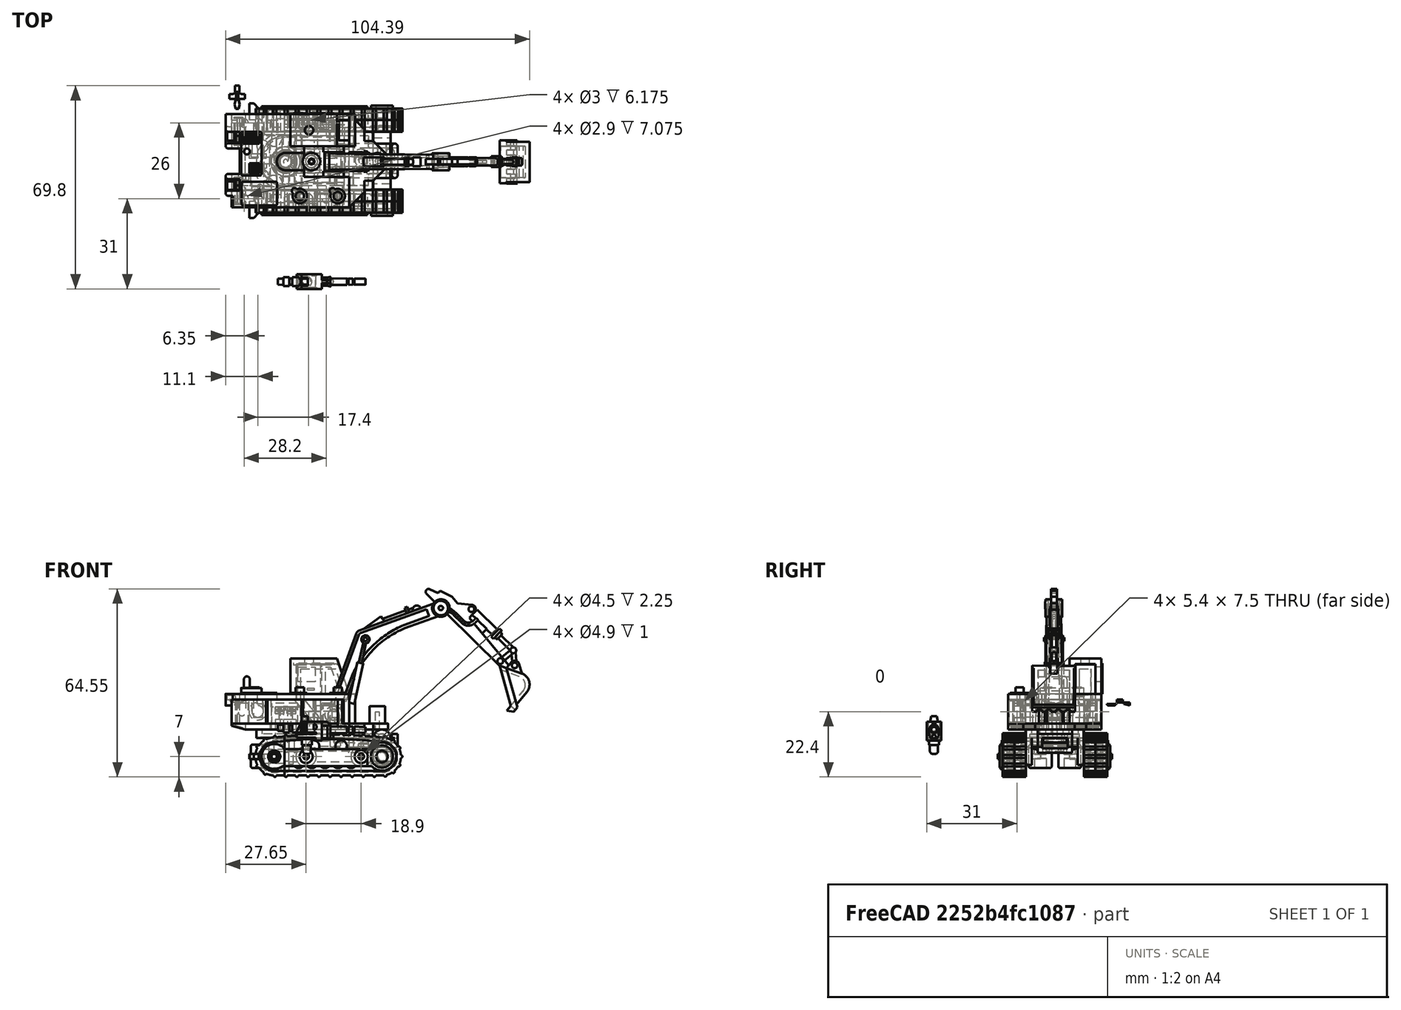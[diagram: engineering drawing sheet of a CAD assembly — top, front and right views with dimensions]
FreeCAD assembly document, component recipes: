
FREECAD ASSEMBLY — COMPONENT RECIPES ("Scavanger")

This assembly document has 15 components, labeled P0..P14 below (a component is one placed body or linked part). 15 of them carry a construction recipe — the FreeCAD feature program that regenerates the part from scratch, quoted from this document or its linked companion documents; the rest are supplied as boundary geometry only. No exploded tour is included for this assembly.
NOTE — document 2 of 4 of this assembly tour. The two overview renders and the header above are repeated from document 1; the component sections below continue where the previous document stopped.
COMPONENT P2 — recipe-attached ("Lower_Scoop", modeled in this document).
Construction recipe (the document's own serialized feature program — sketch geometry with constraints, then the solid features built on it; lengths are millimeters unless a unit is written):

FEATURE [Sketcher::SketchObject] Sketch065
  ArcFitTolerance = 1e-06
  AttachmentSupport = -> [XY_Plane002]
  FullyConstrained = true
  MakeInternals = false
  MapMode = 5
  sketch-geometry (12):
    g0: LineSegment [constr] StartX=-4e-16 StartY=0 StartZ=0 EndX=50.4 EndY=-4e-16 EndZ=0
    g1: LineSegment StartX=-4e-16 StartY=0 StartZ=0 EndX=25.1943 EndY=11.751 EndZ=0
    g2: LineSegment StartX=50.4 StartY=-4e-16 StartZ=0 EndX=25.1943 EndY=11.751 EndZ=0
    g3: LineSegment StartX=1.9444 StartY=-4.16885 StartZ=0 EndX=12.9214 EndY=0.950952 EndZ=0
    g4: ArcOfCircle CenterX=25.1943 CenterY=-29.2294 CenterZ=0 NormalX=0 NormalY=0 NormalZ=1 AngleXU=0 Radius=32.5803 StartAngle=1.18457 EndAngle=1.95703
    g5: LineSegment StartX=37.4673 StartY=0.950952 StartZ=0 EndX=48.4563 EndY=-4.16918 EndZ=0
    g6: LineSegment [constr] StartX=50.4 StartY=-4e-16 StartZ=0 EndX=48.4563 EndY=-4.16918 EndZ=0
    g7: LineSegment [constr] StartX=-4e-16 StartY=0 StartZ=0 EndX=1.9444 EndY=-4.16885 EndZ=0
    g8: LineSegment [constr] StartX=25.1943 StartY=-29.2294 StartZ=0 EndX=25.1943 EndY=3.35095 EndZ=0
    g9: LineSegment [constr] StartX=25.1943 StartY=3.35095 StartZ=0 EndX=25.1943 EndY=11.751 EndZ=0
    g10: ArcOfCircle CenterX=51.1739 CenterY=-2.89846 CenterZ=0 NormalX=0 NormalY=0 NormalZ=1 AngleXU=0 Radius=3 StartAngle=3.57898 EndAngle=8.1149
    g11: ArcOfCircle CenterX=-0.773401 CenterY=-2.89859 CenterZ=0 NormalX=0 NormalY=0 NormalZ=1 AngleXU=0 Radius=3 StartAngle=1.31005 EndAngle=5.84597
  constraints (35):
    c: Coincident(g0,g-1)
    c: PointOnObject(g0,g-1)
    c: Coincident(g1,g0)
    c: Coincident(g2,g0)
    c: Coincident(g2,g1)
    c: Angle(g1,g2) = 2.26893
    c: DistanceX(g0,g0) = 50.4
    c: Distance(g1) = 27.8
    c: Distance(g2) = 27.8102
    c: Coincident(g4,g3)
    c: Coincident(g5,g4)
    c: Coincident(g6,g0)
    c: Coincident(g6,g5)
    c: Distance(g6) = 4.6
    c: Coincident(g7,g0)
    c: Coincident(g7,g3)
    c: Distance(g7) = 4.6
    c: Coincident(g8,g4)
    c: PointOnObject(g8,g4)
    c: Vertical(g8)
    c: Coincident(g9,g8)
    c: Coincident(g9,g1)
    c: Vertical(g9)
    c: DistanceY(g9,g9) = 8.4
    c: Angle(g7,g1) = 1.5708
    c: Angle(g3,g7) = 1.5708
    c: DistanceY(g4,g3) = 0
    c: Angle(g2,g6) = 1.5708
    c: DistanceY(g3,g8) = 2.4
    c: Coincident(g10,g0)
    c: Coincident(g10,g5)
    c: Diameter(g10) = 6
    c: Coincident(g11,g0)
    c: Coincident(g11,g3)
    c: Diameter(g11) = 6
FEATURE [PartDesign::Pad] Pad038
  Direction = (0,0,1)
  Length = 5.6
  Length2 = 10
  Profile = -> Sketch065
  ReferenceAxis = -> Sketch065 [N_Axis]
  Refine = true
  Suppressed = false
  Type = 0
FEATURE [PartDesign::Fillet] Fillet003
  Base = -> Pad038 [Edge2]
  BaseFeature = -> Pad038
  Radius = 2
  Refine = true
  SupportTransform = false
  Suppressed = false
  UseAllEdges = false
FEATURE [Sketcher::SketchObject] Sketch066
  ArcFitTolerance = 1e-06
  AttachmentSupport = -> [Fillet003]
  ExternalGeometry = -> [Fillet003]
  FullyConstrained = true
  MakeInternals = false
  MapMode = 5
  Placement = pos=(0,0,0) rot=(1,0,0;3.14159rad)
  sketch-geometry (1):
    g0: Circle CenterX=51.1739 CenterY=2.89846 CenterZ=0 NormalX=0 NormalY=0 NormalZ=1 AngleXU=0 Radius=3
  constraints (2):
    c: Coincident(g0,g-3)
    c: Equal(g0,g-3)
FEATURE [PartDesign::Pad] Pad039
  BaseFeature = -> Fillet003
  Direction = (0,0,-1)
  Length = 0.25
  Length2 = 10
  Profile = -> Sketch066
  ReferenceAxis = -> Sketch066 [N_Axis]
  Refine = true
  Suppressed = false
  Type = 0
FEATURE [Sketcher::SketchObject] Sketch067
  ArcFitTolerance = 1e-06
  AttachmentSupport = -> [Pad039]
  ExternalGeometry = -> [Pad039]
  FullyConstrained = true
  MakeInternals = false
  MapMode = 5
  Placement = pos=(0,0,5.6) rot=(0,0,1;0rad)
  sketch-geometry (1):
    g0: Circle CenterX=51.1739 CenterY=-2.89846 CenterZ=0 NormalX=0 NormalY=0 NormalZ=1 AngleXU=0 Radius=3
  constraints (2):
    c: Coincident(g0,g-4)
    c: Equal(g0,g-4)
FEATURE [PartDesign::Pad] Pad040
  BaseFeature = -> Pad039
  Direction = (0,0,1)
  Length = 0.25
  Length2 = 10
  Profile = -> Sketch067
  ReferenceAxis = -> Sketch067 [N_Axis]
  Refine = true
  Suppressed = false
  Type = 0
FEATURE [Sketcher::SketchObject] Sketch068
  ArcFitTolerance = 1e-06
  AttachmentSupport = -> [Pad040]
  ExternalGeometry = -> [Pad040]
  FullyConstrained = true
  MakeInternals = false
  MapMode = 5
  Placement = pos=(0,0,5.6) rot=(0,0,1;0rad)
  sketch-geometry (1):
    g0: Circle CenterX=-0.773401 CenterY=-2.89859 CenterZ=0 NormalX=0 NormalY=0 NormalZ=1 AngleXU=0 Radius=3
  constraints (2):
    c: Coincident(g0,g-3)
    c: Equal(g0,g-3)
FEATURE [PartDesign::Pad] Pad041
  BaseFeature = -> Pad040
  Direction = (0,0,1)
  Length = 0.1
  Length2 = 10
  Profile = -> Sketch068
  ReferenceAxis = -> Sketch068 [N_Axis]
  Refine = true
  Suppressed = false
  Type = 0
FEATURE [Sketcher::SketchObject] Sketch069
  ArcFitTolerance = 1e-06
  AttachmentSupport = -> [Pad041]
  ExternalGeometry = -> [Pad041]
  FullyConstrained = true
  MakeInternals = false
  MapMode = 5
  Placement = pos=(0,0,0) rot=(1,0,0;3.14159rad)
  sketch-geometry (1):
    g0: Circle CenterX=-0.773401 CenterY=2.89859 CenterZ=0 NormalX=0 NormalY=0 NormalZ=1 AngleXU=0 Radius=3
  constraints (2):
    c: Coincident(g0,g-3)
    c: Equal(g0,g-3)
FEATURE [PartDesign::Pad] Pad042
  BaseFeature = -> Pad041
  Direction = (0,0,-1)
  Length = 0.1
  Length2 = 10
  Profile = -> Sketch069
  ReferenceAxis = -> Sketch069 [N_Axis]
  Refine = true
  Suppressed = false
  Type = 0
FEATURE [Sketcher::SketchObject] Sketch070
  ArcFitTolerance = 1e-06
  AttachmentSupport = -> [Pad042]
  ExternalGeometry = -> [Pad042]
  FullyConstrained = false
  MakeInternals = false
  MapMode = 5
  Placement = pos=(0,0,0) rot=(1,0,0;3.14159rad)
  sketch-geometry (4):
    g0: LineSegment StartX=24.0163 StartY=-5.17817 StartZ=0 EndX=24.0163 EndY=-6.67308 EndZ=0
    g1: LineSegment StartX=24.0163 StartY=-6.67308 StartZ=0 EndX=26.3302 EndY=-6.67308 EndZ=0
    g2: LineSegment StartX=26.3302 StartY=-6.67308 StartZ=0 EndX=26.3302 EndY=-5.17817 EndZ=0
    g3: LineSegment StartX=26.3302 StartY=-5.17817 StartZ=0 EndX=24.0163 EndY=-5.17817 EndZ=0
  constraints (8):
    c: Coincident(g0,g1)
    c: Coincident(g1,g2)
    c: Coincident(g2,g3)
    c: Coincident(g3,g0)
    c: Vertical(g0)
    c: Vertical(g2)
    c: Horizontal(g1)
    c: Horizontal(g3)
FEATURE [PartDesign::Pad] Pad043
  BaseFeature = -> Pad042
  Direction = (0,0,-1)
  Length = 1
  Length2 = 10
  Profile = -> Sketch070
  ReferenceAxis = -> Sketch070 [N_Axis]
  Refine = true
  Suppressed = false
  Type = 0
FEATURE [Sketcher::SketchObject] Sketch071
  ArcFitTolerance = 1e-06
  AttachmentOffset = pos=(0,0,-8) rot=(0,0,1;0rad)
  AttachmentSupport = -> [Pad043]
  ExternalGeometry = -> [Pad043]
  FullyConstrained = true
  MakeInternals = false
  MapMode = 5
  Placement = pos=(0,13.1782,-1.8e-15) rot=(1,0,0;1.5708rad)
  sketch-geometry (10):
    g0: LineSegment StartX=50.4 StartY=1e-16 StartZ=0 EndX=50.4 EndY=-2 EndZ=0
    g1: LineSegment StartX=50.4 StartY=-2 StartZ=0 EndX=0 EndY=-2 EndZ=0
    g2: LineSegment StartX=0 StartY=-2 StartZ=0 EndX=0 EndY=0 EndZ=0
    g3: LineSegment StartX=0 StartY=0 StartZ=0 EndX=-4e-16 EndY=0.4 EndZ=0
    g4: LineSegment StartX=-4e-16 StartY=0.4 StartZ=0 EndX=50.4 EndY=1e-16 EndZ=0
    g5: LineSegment StartX=0 StartY=5.6 StartZ=0 EndX=-4e-16 EndY=5.2 EndZ=0
    g6: LineSegment StartX=-4e-16 StartY=5.2 StartZ=0 EndX=50.4 EndY=5.6 EndZ=0
    g7: LineSegment StartX=50.4 StartY=5.6 StartZ=0 EndX=50.4 EndY=7.6 EndZ=0
    g8: LineSegment StartX=50.4 StartY=7.6 StartZ=0 EndX=0 EndY=7.6 EndZ=0
    g9: LineSegment StartX=0 StartY=5.6 StartZ=0 EndX=0 EndY=7.6 EndZ=0
  constraints (26):
    c: Coincident(g0,g-5)
    c: Vertical(g0)
    c: Coincident(g1,g0)
    c: Horizontal(g1)
    c: Coincident(g2,g1)
    c: Coincident(g2,g-1)
    c: Vertical(g2)
    c: Coincident(g3,g2)
    c: PointOnObject(g3,g-3)
    c: Coincident(g4,g3)
    c: Coincident(g4,g0)
    c: DistanceY(g3,g3) = 0.4
    c: DistanceY(g2,g2) = 2
    c: PointOnObject(g5,g-3)
    c: Coincident(g6,g5)
    c: DistanceY(g5,g5) = 0.4
    c: Coincident(g7,g6)
    c: Vertical(g7)
    c: Coincident(g8,g7)
    c: PointOnObject(g8,g-2)
    c: Horizontal(g8)
    c: Coincident(g9,g5)
    c: Coincident(g9,g8)
    c: DistanceY(g9,g9) = 2
    c: Coincident(g5,g-8)
    c: Coincident(g6,g-6)
FEATURE [PartDesign::Pocket] Pocket028
  BaseFeature = -> Pad043
  Direction = (0,1,-2e-16)
  Length = 22
  Length2 = 5
  Profile = -> Sketch071
  ReferenceAxis = -> Sketch071 [N_Axis]
  Refine = true
  Reversed = true
  Suppressed = false
  Type = 0
FEATURE [Sketcher::SketchObject] Sketch072
  ArcFitTolerance = 1e-06
  AttachmentSupport = -> [Pocket028]
  ExternalGeometry = -> [Pocket028]
  FullyConstrained = true
  MakeInternals = false
  MapMode = 5
  Placement = pos=(0,0,5.85) rot=(0,0,1;0rad)
  sketch-geometry (1):
    g0: Circle CenterX=51.1739 CenterY=-2.89846 CenterZ=0 NormalX=0 NormalY=0 NormalZ=1 AngleXU=0 Radius=3
  constraints (2):
    c: Coincident(g0,g-3)
    c: Equal(g0,g-3)
FEATURE [PartDesign::Pad] Pad044
  BaseFeature = -> Pocket028
  Direction = (0,0,1)
  Length = 6.1
  Length2 = 10
  Profile = -> Sketch072
  ReferenceAxis = -> Sketch072 [N_Axis]
  Refine = true
  Reversed = true
  Suppressed = false
  Type = 0
FEATURE [Sketcher::SketchObject] Sketch073
  ArcFitTolerance = 1e-06
  AttachmentSupport = -> [Pad044]
  ExternalGeometry = -> [Pad044]
  FullyConstrained = true
  MakeInternals = false
  MapMode = 5
  Placement = pos=(0,0,5.7) rot=(0,0,1;0rad)
  sketch-geometry (1):
    g0: Circle CenterX=-0.773401 CenterY=-2.89859 CenterZ=0 NormalX=0 NormalY=0 NormalZ=1 AngleXU=0 Radius=3
  constraints (2):
    c: Coincident(g0,g-3)
    c: Equal(g0,g-3)
FEATURE [PartDesign::Pad] Pad045
  BaseFeature = -> Pad044
  Direction = (0,0,1)
  Length = 5.8
  Length2 = 10
  Profile = -> Sketch073
  ReferenceAxis = -> Sketch073 [N_Axis]
  Refine = true
  Reversed = true
  Suppressed = false
  Type = 0
FEATURE [PartDesign::Pad] Pad046
  BaseFeature = -> Pad045
  Direction = (0,0,-1)
  Length = 0.25
  Length2 = 10
  Profile = -> Pad045 [Face1]
  Refine = true
  Suppressed = false
  Type = 0
FEATURE [PartDesign::Pad] Pad047
  BaseFeature = -> Pad046
  Direction = (0,0,1)
  Length = 0.25
  Length2 = 10
  Profile = -> Pad046 [Face1]
  Refine = true
  Suppressed = false
  Type = 0
FEATURE [Sketcher::SketchObject] Sketch074
  ArcFitTolerance = 1e-06
  AttachmentSupport = -> [Pad047]
  ExternalGeometry = -> [Pad047]
  FullyConstrained = true
  MakeInternals = false
  MapMode = 5
  Placement = pos=(0,0,6.1) rot=(0,0,1;0rad)
  sketch-geometry (1):
    g0: Circle CenterX=51.1739 CenterY=-2.89846 CenterZ=0 NormalX=0 NormalY=0 NormalZ=1 AngleXU=0 Radius=1.9
  constraints (2):
    c: Coincident(g0,g-3)
    c: Radius(g0) = 1.9
FEATURE [PartDesign::Pad] Pad048
  BaseFeature = -> Pad047
  Direction = (0,0,1)
  Length = 2
  Length2 = 10
  Profile = -> Sketch074
  ReferenceAxis = -> Sketch074 [N_Axis]
  Refine = true
  Suppressed = false
  Type = 0
FEATURE [Sketcher::SketchObject] Sketch075
  ArcFitTolerance = 1e-06
  AttachmentSupport = -> [Pad048]
  ExternalGeometry = -> [Pad048]
  FullyConstrained = true
  MakeInternals = false
  MapMode = 5
  Placement = pos=(0,0,-0.5) rot=(1,0,0;3.14159rad)
  sketch-geometry (1):
    g0: Circle CenterX=51.1739 CenterY=2.89846 CenterZ=0 NormalX=0 NormalY=0 NormalZ=1 AngleXU=0 Radius=1.9
  constraints (2):
    c: Coincident(g0,g-3)
    c: Radius(g0) = 1.9
FEATURE [PartDesign::Pad] Pad049
  BaseFeature = -> Pad048
  Direction = (0,0,-1)
  Length = 2
  Length2 = 10
  Profile = -> Sketch075
  ReferenceAxis = -> Sketch075 [N_Axis]
  Refine = true
  Suppressed = false
  Type = 0
FEATURE [Sketcher::SketchObject] Sketch076
  ArcFitTolerance = 1e-06
  AttachmentSupport = -> [Pad049]
  ExternalGeometry = -> [Pad049]
  FullyConstrained = true
  MakeInternals = false
  MapMode = 5
  Placement = pos=(0,0,5.7) rot=(0,0,1;0rad)
  sketch-geometry (1):
    g0: Circle CenterX=-0.773401 CenterY=-2.89859 CenterZ=0 NormalX=0 NormalY=0 NormalZ=1 AngleXU=0 Radius=0.75
  constraints (2):
    c: Radius(g0) = 0.75
    c: Coincident(g0,g-3)
FEATURE [PartDesign::Pocket] Pocket029
  BaseFeature = -> Pad049
  Direction = (0,0,-1)
  Length = 6
  Length2 = 5
  Profile = -> Sketch076
  ReferenceAxis = -> Sketch076 [N_Axis]
  Refine = true
  Suppressed = false
  Type = 0
FEATURE [Sketcher::SketchObject] Sketch077
  ArcFitTolerance = 1e-06
  AttachmentSupport = -> [Pocket029]
  ExternalGeometry = -> [Pocket029]
  FullyConstrained = true
  MakeInternals = false
  MapMode = 5
  Placement = pos=(0.0031744,1e-16,0.399975) rot=(0.999992,0,-0.003968;3.14159rad)
  sketch-geometry (14):
    g0: LineSegment StartX=2.22247 StartY=2.82018 StartZ=0 EndX=12.4102 EndY=-1.93134 EndZ=0
    g1: ArcOfCircle CenterX=25.192 CenterY=29.2294 CenterZ=0 NormalX=0 NormalY=0 NormalZ=1 AngleXU=0 Radius=33.6803 StartAngle=4.32313 EndAngle=5.05713
    g2: LineSegment StartX=36.5742 StartY=-2.46935 StartZ=0 EndX=48.1725 EndY=2.93448 EndZ=0
    g3: ArcOfCircle CenterX=51.1722 CenterY=2.89849 CenterZ=0 NormalX=0 NormalY=0 NormalZ=1 AngleXU=0 Radius=3 StartAngle=3.12959 EndAngle=4.02604
    g4: LineSegment StartX=49.2711 StartY=0.577787 StartZ=0 EndX=25.6148 EndY=-10.4505 EndZ=0
    g5: ArcOfCircle CenterX=25.1922 CenterY=-9.5442 CenterZ=0 NormalX=0 NormalY=0 NormalZ=1 AngleXU=0 Radius=1.00001 StartAngle=4.27602 EndAngle=5.14876
    g6: LineSegment StartX=24.7695 StartY=-10.4505 StartZ=0 EndX=1.12424 EndY=0.577594 EndZ=0
    g7: LineSegment [constr] StartX=3.75384 StartY=3.32348 StartZ=0 EndX=3.28744 EndY=2.32348 EndZ=0
    g8: ArcOfCircle CenterX=-0.776505 CenterY=2.89862 CenterZ=0 NormalX=0 NormalY=0 NormalZ=1 AngleXU=0 Radius=3 StartAngle=5.39856 EndAngle=6.25703
    g9: LineSegment [constr] StartX=2.23467 StartY=0.0596903 StartZ=0 EndX=1.81199 EndY=-0.846586 EndZ=0
    g10: LineSegment [constr] StartX=47.0641 StartY=2.41808 StartZ=0 EndX=46.6418 EndY=3.32453 EndZ=0
    g11: LineSegment [constr] StartX=48.1632 StartY=0.0612903 StartZ=0 EndX=48.5857 EndY=-0.845059 EndZ=0
    g12: LineSegment [constr] StartX=25.192 StartY=29.2294 StartZ=0 EndX=25.192 EndY=-3.35095 EndZ=0
    g13: LineSegment [constr] StartX=25.192 StartY=-3.35095 StartZ=0 EndX=25.192 EndY=-4.45095 EndZ=0
  constraints (47):
    c: PointOnObject(g0,g-10)
    c: Coincident(g1,g0)
    c: Coincident(g2,g1)
    c: PointOnObject(g2,g-3)
    c: Coincident(g3,g2)
    c: Coincident(g4,g3)
    c: Coincident(g5,g4)
    c: Coincident(g6,g5)
    c: PointOnObject(g6,g-10)
    c: Tangent(g3,g-3) = -1.5708
    c: Coincident(g1,g-6)
    c: PointOnObject(g7,g-9)
    c: PointOnObject(g7,g0)
    c: Perpendicular(g7,g-9)
    c: DistanceY(g7,g7) = 1
    c: Coincident(g8,g6)
    c: Coincident(g8,g0)
    c: PointOnObject(g9,g6)
    c: PointOnObject(g9,g-8)
    c: Perpendicular(g-8,g9)
    c: Parallel(g0,g-9)
    c: Parallel(g6,g-8)
    c: Parallel(g2,g-4)
    c: Parallel(g4,g-5)
    c: Distance(g-1,g9) = 2
    c: Distance(g7,g-9) = 2
    c: Distance(g9) = 1
    c: Coincident(g5,g-7)
    c: Radius(g8) = 3
    c: PointOnObject(g10,g2)
    c: PointOnObject(g10,g-4)
    c: Perpendicular(g-4,g10)
    c: Distance(g-4,g10) = 2
    c: Distance(g10) = 1
    c: PointOnObject(g11,g4)
    c: PointOnObject(g11,g-5)
    c: Perpendicular(g4,g11)
    c: Distance(g11,g-5) = 2
    c: Distance(g11) = 1
    c: DistanceY(g4,g5) = 0
    c: Coincident(g12,g1)
    c: PointOnObject(g12,g-6)
    c: Vertical(g12)
    c: Coincident(g13,g12)
    c: PointOnObject(g13,g1)
    c: Vertical(g13)
    c: DistanceY(g13,g13) = 1.1
FEATURE [PartDesign::Pocket] Pocket030
  BaseFeature = -> Pocket029
  Direction = (0.00793626,0,0.999969)
  Length = 1
  Length2 = 5
  Profile = -> Sketch077
  ReferenceAxis = -> Sketch077 [N_Axis]
  Refine = true
  Suppressed = false
  Type = 0
FEATURE [Sketcher::SketchObject] Sketch078
  ArcFitTolerance = 1e-06
  AttachmentSupport = -> [Pocket030]
  ExternalGeometry = -> [Pocket030]
  FullyConstrained = true
  MakeInternals = false
  MapMode = 5
  Placement = pos=(-0.0412672,1.1e-15,5.19967) rot=(0,-1,0;0.007936rad)
  sketch-geometry (16):
    g0: LineSegment StartX=24.7884 StartY=10.4386 StartZ=0 EndX=1.16868 EndY=-0.577594 EndZ=0
    g1: ArcOfCircle CenterX=-0.732063 CenterY=-2.89862 CenterZ=0 NormalX=0 NormalY=0 NormalZ=1 AngleXU=0 Radius=3 StartAngle=6.27142 EndAngle=7.16781
    g2: LineSegment StartX=2.26773 StartY=-2.93391 StartZ=0 EndX=13.015 EndY=2.0786 EndZ=0
    g3: ArcOfCircle CenterX=25.2362 CenterY=-29.649 CenterZ=0 NormalX=0 NormalY=0 NormalZ=1 AngleXU=0 Radius=34 StartAngle=1.20312 EndAngle=1.93847
    g4: ArcOfCircle CenterX=25.2366 CenterY=9.54034 CenterZ=0 NormalX=0 NormalY=0 NormalZ=1 AngleXU=0 Radius=1.00385 StartAngle=1.16095 EndAngle=2.0336
    g5: LineSegment StartX=25.6366 StartY=10.4611 StartZ=0 EndX=49.3155 EndY=-0.577787 EndZ=0
    g6: LineSegment StartX=37.4573 StartY=2.0786 StartZ=0 EndX=48.2169 EndY=-2.93448 EndZ=0
    g7: ArcOfCircle CenterX=51.2167 CenterY=-2.89849 CenterZ=0 NormalX=0 NormalY=0 NormalZ=1 AngleXU=0 Radius=3 StartAngle=2.25714 EndAngle=3.15359
    g8: LineSegment [constr] StartX=2.27651 StartY=-0.0609062 StartZ=0 EndX=1.85382 EndY=0.84537 EndZ=0
    g9: LineSegment [constr] StartX=3.3756 StartY=-2.4172 StartZ=0 EndX=3.79829 EndY=-3.32348 EndZ=0
    g10: LineSegment [constr] StartX=48.2076 StartY=-0.0612903 StartZ=0 EndX=48.6302 EndY=0.845059 EndZ=0
    g11: LineSegment [constr] StartX=47.1086 StartY=-2.41808 StartZ=0 EndX=46.6862 EndY=-3.32453 EndZ=0
    g12: LineSegment [constr] StartX=25.2366 StartY=9.54034 StartZ=0 EndX=25.2366 EndY=10.5442 EndZ=0
    g13: LineSegment [constr] StartX=25.2366 StartY=10.5442 StartZ=0 EndX=25.2366 EndY=11.5442 EndZ=0
    g14: LineSegment [constr] StartX=25.2364 StartY=-29.2294 StartZ=0 EndX=25.2364 EndY=3.35095 EndZ=0
    g15: LineSegment [constr] StartX=25.2364 StartY=3.35095 StartZ=0 EndX=25.2364 EndY=4.35095 EndZ=0
  constraints (56):
    c: Coincident(g1,g0)
    c: Coincident(g2,g1)
    c: Coincident(g3,g2)
    c: Coincident(g4,g0)
    c: Coincident(g5,g4)
    c: PointOnObject(g5,g-8)
    c: Coincident(g6,g3)
    c: PointOnObject(g6,g-8)
    c: Coincident(g7,g6)
    c: Coincident(g7,g5)
    c: PointOnObject(g0,g-10)
    c: PointOnObject(g1,g-10)
    c: PointOnObject(g8,g0)
    c: PointOnObject(g8,g-4)
    c: PointOnObject(g9,g2)
    c: PointOnObject(g9,g-11)
    c: Perpendicular(g0,g8)
    c: Perpendicular(g-11,g9)
    c: Parallel(g2,g-11)
    c: Parallel(g0,g-4)
    c: Distance(g9,g-11) = 2
    c: Distance(g8,g-4) = 2
    c: Distance(g8) = 1
    c: Distance(g9) = 1
    c: Radius(g1) = 3
    c: PointOnObject(g10,g5)
    c: PointOnObject(g10,g-3)
    c: PointOnObject(g11,g6)
    c: PointOnObject(g11,g-7)
    c: Parallel(g5,g-3)
    c: Parallel(g6,g-7)
    c: Perpendicular(g-7,g11)
    c: Perpendicular(g-3,g10)
    c: Distance(g-3,g10) = 2
    c: Distance(g11,g-7) = 2
    c: Distance(g11) = 1
    c: Distance(g10) = 1
    c: Radius(g7) = 3
    c: Coincident(g12,g4)
    c: PointOnObject(g12,g4)
    c: Vertical(g12)
    c: Coincident(g13,g12)
    c: PointOnObject(g13,g-6)
    c: Vertical(g13)
    c: DistanceY(g13,g13) = 1
    c: DistanceX(g-6,g4) = 0
    c: DistanceX(g12,g4) = 0.4
    c: Coincident(g14,g-5)
    c: PointOnObject(g14,g-5)
    c: Vertical(g14)
    c: Coincident(g15,g14)
    c: PointOnObject(g15,g3)
    c: Vertical(g15)
    c: DistanceY(g15,g15) = 1
    c: Radius(g3) = 34
    c: DistanceY(g2,g3) = 0
FEATURE [PartDesign::Pocket] Pocket031
  BaseFeature = -> Pocket030
  Direction = (0.00793626,0,-0.999969)
  Length = 1
  Length2 = 5
  Profile = -> Sketch078
  ReferenceAxis = -> Sketch078 [N_Axis]
  Refine = true
  Suppressed = false
  Type = 0
FEATURE [Sketcher::SketchObject] Sketch079
  ArcFitTolerance = 1e-06
  AttachmentSupport = -> [Pocket031]
  ExternalGeometry = -> [Pocket031]
  FullyConstrained = true
  MakeInternals = false
  MapMode = 5
  Placement = pos=(0,0,-0.1) rot=(1,0,0;3.14159rad)
  sketch-geometry (2):
    g0: Circle CenterX=-0.773401 CenterY=2.89859 CenterZ=0 NormalX=0 NormalY=0 NormalZ=1 AngleXU=0 Radius=0.75
    g1: Circle CenterX=-0.773401 CenterY=2.89859 CenterZ=0 NormalX=0 NormalY=0 NormalZ=1 AngleXU=0 Radius=2.5
  constraints (4):
    c: Coincident(g0,g-3)
    c: Equal(g0,g-3)
    c: Coincident(g1,g0)
    c: Radius(g1) = 2.5
FEATURE [PartDesign::Pocket] Pocket032
  BaseFeature = -> Pocket031
  Direction = (0,0,1)
  Length = 1
  Length2 = 5
  Profile = -> Sketch079
  ReferenceAxis = -> Sketch079 [N_Axis]
  Refine = true
  Suppressed = false
  Type = 0
FEATURE [Sketcher::SketchObject] Sketch080
  ArcFitTolerance = 1e-06
  AttachmentSupport = -> [Pocket032]
  ExternalGeometry = -> [Pocket032]
  FullyConstrained = true
  MakeInternals = false
  MapMode = 5
  Placement = pos=(0,0,5.7) rot=(0,0,1;0rad)
  sketch-geometry (2):
    g0: Circle CenterX=-0.773401 CenterY=-2.89859 CenterZ=0 NormalX=0 NormalY=0 NormalZ=1 AngleXU=0 Radius=0.75
    g1: Circle CenterX=-0.773401 CenterY=-2.89859 CenterZ=0 NormalX=0 NormalY=0 NormalZ=1 AngleXU=0 Radius=2.5
  constraints (4):
    c: Coincident(g0,g-3)
    c: Equal(g0,g-3)
    c: Coincident(g1,g0)
    c: Radius(g1) = 2.5
FEATURE [PartDesign::Pocket] Pocket033
  BaseFeature = -> Pocket032
  Direction = (0,0,-1)
  Length = 1
  Length2 = 5
  Profile = -> Sketch080
  ReferenceAxis = -> Sketch080 [N_Axis]
  Refine = true
  Suppressed = false
  Type = 0
FEATURE [Sketcher::SketchObject] Sketch081
  ArcFitTolerance = 1e-06
  AttachmentOffset = pos=(0,0,-1.9) rot=(0,0,1;0rad)
  AttachmentSupport = -> [Pocket033]
  ExternalGeometry = -> [Pocket033]
  FullyConstrained = true
  MakeInternals = false
  MapMode = 5
  Placement = pos=(0,0,3.8) rot=(0,0,1;0rad)
  sketch-geometry (1):
    g0: Circle CenterX=-0.773401 CenterY=-2.89859 CenterZ=0 NormalX=0 NormalY=0 NormalZ=1 AngleXU=0 Radius=3
  constraints (2):
    c: Coincident(g0,g-3)
    c: Equal(g0,g-3)
FEATURE [PartDesign::Pocket] Pocket034
  BaseFeature = -> Pocket033
  Direction = (0,0,-1)
  Length = 2
  Length2 = 5
  Profile = -> Sketch081
  ReferenceAxis = -> Sketch081 [N_Axis]
  Refine = true
  Suppressed = false
  Type = 0
FEATURE [Sketcher::SketchObject] Sketch082
  ArcFitTolerance = 1e-06
  AttachmentSupport = -> [Pocket034]
  ExternalGeometry = -> [Pocket034]
  FullyConstrained = true
  MakeInternals = false
  MapMode = 5
  Placement = pos=(-0.033331,0,4.1997) rot=(0,-1,0;0.007936rad)
  sketch-geometry (4):
    g0: LineSegment StartX=1.16868 StartY=-0.577594 StartZ=0 EndX=2.98123 EndY=0.267777 EndZ=0
    g1: LineSegment StartX=2.26773 StartY=-2.93391 StartZ=0 EndX=4.08023 EndY=-2.08857 EndZ=0
    g2: LineSegment StartX=2.98123 StartY=0.267777 StartZ=0 EndX=4.08023 EndY=-2.08857 EndZ=0
    g3: ArcOfCircle CenterX=-0.732063 CenterY=-2.89862 CenterZ=0 NormalX=0 NormalY=0 NormalZ=1 AngleXU=0 Radius=3 StartAngle=6.27142 EndAngle=7.16781
  constraints (11):
    c: Coincident(g0,g-3)
    c: PointOnObject(g0,g-3)
    c: Coincident(g1,g-5)
    c: PointOnObject(g1,g-5)
    c: Coincident(g2,g0)
    c: Coincident(g2,g1)
    c: Coincident(g3,g-3)
    c: Coincident(g3,g1)
    c: Radius(g3) = 3
    c: Perpendicular(g2,g0)
    c: Distance(g0) = 2
FEATURE [PartDesign::Pad] Pad050
  BaseFeature = -> Pocket034
  Direction = (-0.00793626,0,0.999969)
  Length = 1
  Length2 = 10
  Profile = -> Sketch082
  ReferenceAxis = -> Sketch082 [N_Axis]
  Refine = true
  Suppressed = false
  Type = 0
FEATURE [Sketcher::SketchObject] Sketch083
  ArcFitTolerance = 1e-06
  AttachmentSupport = -> [Pad050]
  ExternalGeometry = -> [Pad050]
  FullyConstrained = true
  MakeInternals = false
  MapMode = 5
  Placement = pos=(0.0111107,0,1.39994) rot=(0.999992,0,-0.003968;3.14159rad)
  sketch-geometry (4):
    g0: LineSegment StartX=2.22247 StartY=2.82018 StartZ=0 EndX=4.03502 EndY=1.97481 EndZ=0
    g1: LineSegment StartX=1.12424 StartY=0.577594 StartZ=0 EndX=2.97974 EndY=-0.287809 EndZ=0
    g2: LineSegment StartX=2.97974 StartY=-0.287809 StartZ=0 EndX=4.03502 EndY=1.97481 EndZ=0
    g3: ArcOfCircle CenterX=-0.776505 CenterY=2.89862 CenterZ=0 NormalX=0 NormalY=0 NormalZ=1 AngleXU=0 Radius=3 StartAngle=5.39856 EndAngle=6.25703
  constraints (11):
    c: Coincident(g0,g-4)
    c: PointOnObject(g0,g-3)
    c: Coincident(g1,g-5)
    c: PointOnObject(g1,g-5)
    c: Coincident(g2,g1)
    c: Coincident(g2,g0)
    c: Coincident(g3,g0)
    c: Coincident(g3,g-5)
    c: Radius(g3) = 3
    c: Perpendicular(g2,g0)
    c: Distance(g0) = 2
FEATURE [PartDesign::Pad] Pad051
  BaseFeature = -> Pad050
  Direction = (-0.00793626,0,-0.999969)
  Length = 1
  Length2 = 10
  Profile = -> Sketch083
  ReferenceAxis = -> Sketch083 [N_Axis]
  Refine = true
  Suppressed = false
  Type = 0
FEATURE [Sketcher::SketchObject] Sketch084
  ArcFitTolerance = 1e-06
  AttachmentOffset = pos=(0,0,-1) rot=(0,0,1;0rad)
  AttachmentSupport = -> [Pad051]
  ExternalGeometry = -> [Pad051]
  FullyConstrained = true
  MakeInternals = false
  MapMode = 5
  Placement = pos=(0,0,5.1) rot=(0,0,1;0rad)
  sketch-geometry (1):
    g0: Circle CenterX=25.1945 CenterY=7.74034 CenterZ=0 NormalX=0 NormalY=0 NormalZ=1 AngleXU=0 Radius=1.4
  constraints (3):
    c: Diameter(g0) = 2.8
    c: DistanceX(g0,g-3) = 0
    c: DistanceY(g0,g-3) = 1.8
FEATURE [PartDesign::Pad] Pad052
  BaseFeature = -> Pad051
  Direction = (0,0,1)
  Length = 4.5
  Length2 = 10
  Profile = -> Sketch084
  ReferenceAxis = -> Sketch084 [N_Axis]
  Refine = true
  Reversed = true
  Suppressed = false
  Type = 0
FEATURE [Sketcher::SketchObject] Sketch085
  ArcFitTolerance = 1e-06
  AttachmentSupport = -> [Pad052]
  ExternalGeometry = -> [Pad052]
  FullyConstrained = true
  MakeInternals = false
  MapMode = 5
  Placement = pos=(0,0,5.1) rot=(0,0,1;0rad)
  sketch-geometry (7):
    g0: LineSegment [constr] StartX=25.1945 StartY=7.74034 StartZ=0 EndX=26.3687 EndY=6.97795 EndZ=0
    g1: LineSegment [constr] StartX=26.3687 StartY=6.97795 StartZ=0 EndX=43.9818 EndY=-4.45796 EndZ=0
    g2: LineSegment StartX=25.1945 StartY=7.74034 StartZ=0 EndX=24.9223 EndY=7.32098 EndZ=0
    g3: LineSegment StartX=24.9223 StartY=7.32098 StartZ=0 EndX=32.2159 EndY=2.58533 EndZ=0
    g4: LineSegment StartX=32.2159 StartY=2.58533 StartZ=0 EndX=32.7605 EndY=3.42405 EndZ=0
    g5: LineSegment StartX=32.7605 StartY=3.42405 StartZ=0 EndX=25.4668 EndY=8.1597 EndZ=0
    g6: LineSegment StartX=25.4668 StartY=8.1597 StartZ=0 EndX=25.1945 EndY=7.74034 EndZ=0
  constraints (20):
    c: Coincident(g0,g-3)
    c: PointOnObject(g0,g-3)
    c: Angle(g0,g-4) = 0.139626
    c: Coincident(g1,g0)
    c: Angle(g0,g1) = 3.14159
    c: Distance(g1) = 21
    c: Coincident(g2,g0)
    c: Coincident(g3,g2)
    c: Coincident(g4,g3)
    c: Coincident(g5,g4)
    c: Coincident(g6,g5)
    c: Coincident(g6,g0)
    c: Parallel(g1,g5)
    c: Parallel(g1,g3)
    c: Distance(g6) = 0.5
    c: Distance(g2) = 0.5
    c: Perpendicular(g2,g0)
    c: Perpendicular(g6,g0)
    c: Perpendicular(g4,g3)
    c: PointOnObject(g3,g-5)
FEATURE [PartDesign::Body] Body002  label="Lower_Scoop"
  AllowCompound = false
  Group = -> [Sketch065,Pad038,Fillet003,Sketch066,Pad039,Sketch067,Pad040,Sketch068,Pad041,Sketch069,Pad042,Sketch070,Pad043,Sketch071,Pocket028,Sketch072,Pad044,Sketch073,Pad045,Pad046,Pad047,Sketch074,Pad048,Sketch075,Pad049,Sketch076,Pocket029,Sketch077,Pocket030,Sketch078,Pocket031,Sketch079,Pocket032,Sketch080,Pocket033,Sketch081,Pocket034,Sketch082,Pad050,Sketch083,Pad051,Sketch084,Pad052,Sketch085,+32 more]
  Origin = -> Origin002
  Placement = pos=(71.32,-19.15,33) rot=(-0.28,0.68,0.68;2.59356rad)
  Tip = -> Chamfer007
COMPONENT P3 — recipe-attached ("Cab", modeled in this document).
Construction recipe (the document's own serialized feature program — sketch geometry with constraints, then the solid features built on it; lengths are millimeters unless a unit is written):

FEATURE [PartDesign::SubShapeBinder] Binder001
  BindCopyOnChange = 0
  BindMode = 0
  ClaimChildren = false
  Context = -> Body003 [Binder001.]
  Fuse = false
  MakeFace = true
  OffsetFill = false
  OffsetIntersection = false
  OffsetJoinType = 0
  OffsetOpenResult = false
  PartialLoad = false
  Refine = true
  Relative = true
  Support = -> [Body[Pocket016.Face64]]
  _Version = 2
FEATURE [Sketcher::SketchObject] Sketch096
  ArcFitTolerance = 1e-06
  AttachmentSupport = -> [Binder001]
  ExternalGeometry = -> [Binder001]
  FullyConstrained = true
  MakeInternals = false
  MapMode = 5
  Placement = pos=(0,-9,0) rot=(0,0.707107,0.707107;3.14159rad)
  sketch-geometry (6):
    g0: LineSegment StartX=-38.8695 StartY=12.15 StartZ=0 EndX=-42.45 EndY=1.99145 EndZ=0
    g1: LineSegment StartX=-42.45 StartY=1.99145 StartZ=0 EndX=-42.45 EndY=0.05 EndZ=0
    g2: LineSegment StartX=-42.45 StartY=0.05 StartZ=0 EndX=-24.35 EndY=0.05 EndZ=0
    g3: LineSegment StartX=-24.35 StartY=0.05 StartZ=0 EndX=-24.35 EndY=12.15 EndZ=0
    g4: LineSegment StartX=-24.35 StartY=12.15 StartZ=0 EndX=-38.8695 EndY=12.15 EndZ=0
    g5: LineSegment [constr] StartX=-42.1204 StartY=2.92651 StartZ=0 EndX=-42.1676 EndY=2.94313 EndZ=0
  constraints (19):
    c: Coincident(g1,g0)
    c: Vertical(g1)
    c: Coincident(g2,g1)
    c: Horizontal(g2)
    c: Coincident(g3,g2)
    c: Vertical(g3)
    c: Coincident(g4,g3)
    c: Coincident(g4,g0)
    c: Horizontal(g4)
    c: Parallel(g-3,g0)
    c: DistanceY(g-5,g2) = 0.05
    c: DistanceX(g2,g-5) = 0.05
    c: DistanceY(g3,g-5) = 0.05
    c: DistanceX(g-6,g1) = 0.05
    c: PointOnObject(g5,g0)
    c: PointOnObject(g5,g-3)
    c: Perpendicular(g5,g-3)
    c: Distance(g5,g-6) = 1
    c: Distance(g5) = 0.05
FEATURE [PartDesign::Pad] Pad068
  Direction = (0,1,-2e-16)
  Length = 1.5
  Length2 = 10
  Profile = -> Sketch096
  ReferenceAxis = -> Sketch096 [N_Axis]
  Refine = true
  Suppressed = false
  Type = 0
FEATURE [Sketcher::SketchObject] Sketch097
  ArcFitTolerance = 1e-06
  AttachmentSupport = -> [Pad068]
  ExternalGeometry = -> [Pad068]
  FullyConstrained = true
  MakeInternals = false
  MapMode = 5
  Placement = pos=(0,-7.5,2.3e-15) rot=(0,0.707107,0.707107;3.14159rad)
  sketch-geometry (11):
    g0: LineSegment StartX=-38.8695 StartY=12.15 StartZ=0 EndX=-42.45 EndY=1.99145 EndZ=0
    g1: LineSegment StartX=-42.45 StartY=1.99145 StartZ=0 EndX=-42.45 EndY=0.05 EndZ=0
    g2: LineSegment StartX=-42.45 StartY=0.05 StartZ=0 EndX=-40.95 EndY=0.05 EndZ=0
    g3: LineSegment StartX=-40.95 StartY=0.05 StartZ=0 EndX=-40.95 EndY=1.73484 EndZ=0
    g4: LineSegment StartX=-40.95 StartY=1.73484 StartZ=0 EndX=-37.8078 EndY=10.65 EndZ=0
    g5: LineSegment StartX=-38.8695 StartY=12.15 StartZ=0 EndX=-24.35 EndY=12.15 EndZ=0
    g6: LineSegment StartX=-24.35 StartY=12.15 StartZ=0 EndX=-24.35 EndY=0.05 EndZ=0
    g7: LineSegment StartX=-24.35 StartY=0.05 StartZ=0 EndX=-25.85 EndY=0.05 EndZ=0
    g8: LineSegment StartX=-25.85 StartY=0.05 StartZ=0 EndX=-25.85 EndY=10.65 EndZ=0
    g9: LineSegment StartX=-25.85 StartY=10.65 StartZ=0 EndX=-37.8078 EndY=10.65 EndZ=0
    g10: LineSegment [constr] StartX=-40.1992 StartY=8.37747 StartZ=0 EndX=-38.7845 EndY=7.87884 EndZ=0
  constraints (29):
    c: Coincident(g0,g-5)
    c: Coincident(g0,g-4)
    c: Coincident(g1,g0)
    c: Coincident(g1,g-7)
    c: Coincident(g2,g1)
    c: PointOnObject(g2,g-7)
    c: DistanceX(g2,g2) = 1.5
    c: Coincident(g3,g2)
    c: Vertical(g3)
    c: Coincident(g4,g3)
    c: Coincident(g5,g0)
    c: Coincident(g5,g-6)
    c: Coincident(g6,g5)
    c: Coincident(g6,g-7)
    c: Coincident(g7,g6)
    c: PointOnObject(g7,g-7)
    c: Coincident(g8,g7)
    c: Vertical(g8)
    c: Coincident(g9,g8)
    c: Coincident(g9,g4)
    c: Horizontal(g9)
    c: Parallel(g0,g4)
    c: DistanceY(g4,g0) = 1.5
    c: DistanceX(g8,g5) = 1.5
    c: PointOnObject(g10,g0)
    c: PointOnObject(g10,g4)
    c: Perpendicular(g10,g0)
    c: Distance(g0,g10) = 4
    c: Distance(g10) = 1.5
FEATURE [PartDesign::Pad] Pad069
  BaseFeature = -> Pad068
  Direction = (0,1,-2e-16)
  Length = 5.4
  Length2 = 10
  Profile = -> Sketch097
  ReferenceAxis = -> Sketch097 [N_Axis]
  Refine = true
  Suppressed = false
  Type = 0
FEATURE [Sketcher::SketchObject] Sketch098
  ArcFitTolerance = 1e-06
  AttachmentSupport = -> [Pad069]
  ExternalGeometry = -> [Pad069]
  FullyConstrained = true
  MakeInternals = false
  MapMode = 5
  Placement = pos=(0,-2.1,5e-16) rot=(0,0.707107,0.707107;3.14159rad)
  sketch-geometry (5):
    g0: LineSegment StartX=-40.95 StartY=0.05 StartZ=0 EndX=-25.85 EndY=0.05 EndZ=0
    g1: LineSegment StartX=-25.85 StartY=0.05 StartZ=0 EndX=-25.85 EndY=10.65 EndZ=0
    g2: LineSegment StartX=-25.85 StartY=10.65 StartZ=0 EndX=-37.8078 EndY=10.65 EndZ=0
    g3: LineSegment StartX=-37.8078 StartY=10.65 StartZ=0 EndX=-40.95 EndY=1.73484 EndZ=0
    g4: LineSegment StartX=-40.95 StartY=1.73484 StartZ=0 EndX=-40.95 EndY=0.05 EndZ=0
  constraints (10):
    c: Coincident(g0,g-3)
    c: Coincident(g0,g-6)
    c: Coincident(g1,g0)
    c: Coincident(g1,g-6)
    c: Coincident(g2,g1)
    c: Coincident(g2,g-5)
    c: Coincident(g3,g2)
    c: Coincident(g3,g-4)
    c: Coincident(g4,g3)
    c: Coincident(g4,g0)
FEATURE [PartDesign::Pad] Pad070
  BaseFeature = -> Pad069
  Direction = (0,1,-2e-16)
  Length = 1.5
  Length2 = 10
  Profile = -> Sketch098
  ReferenceAxis = -> Sketch098 [N_Axis]
  Refine = true
  Reversed = true
  Suppressed = false
  Type = 0
FEATURE [PartDesign::Body] Body003  label="Cab"
  AllowCompound = false
  Group = -> [Binder001,Sketch096,Pad068,Sketch097,Pad069,Sketch098,Pad070]
  Origin = -> Origin003
  Tip = -> Pad070
COMPONENT P4 — recipe-attached ("Upper_Scoop", modeled in this document).
Construction recipe (the document's own serialized feature program — sketch geometry with constraints, then the solid features built on it; lengths are millimeters unless a unit is written):

FEATURE [Sketcher::SketchObject] Sketch099
  ArcFitTolerance = 1e-06
  AttachmentSupport = -> [XY_Plane004]
  FullyConstrained = true
  MakeInternals = false
  MapMode = 5
  sketch-geometry (5):
    g0: LineSegment StartX=4.60348 StartY=-9.77661 StartZ=0 EndX=0 EndY=-13 EndZ=0
    g1: LineSegment StartX=0 StartY=0 StartZ=0 EndX=0 EndY=-13 EndZ=0
    g2: LineSegment StartX=0 StartY=0 StartZ=0 EndX=4.60348 EndY=-3.22339 EndZ=0
    g3: ArcOfCircle CenterX=2.30917 CenterY=-6.5 CenterZ=0 NormalX=0 NormalY=0 NormalZ=1 AngleXU=0 Radius=4 StartAngle=5.32325 EndAngle=7.24312
    g4: GeomPoint [constr] X=9.28296 Y=-6.5 Z=0
  constraints (12):
    c: PointOnObject(g0,g-2)
    c: Coincident(g1,g0)
    c: DistanceY(g1,g1) = 13
    c: Coincident(g2,g1)
    c: PointOnObject(g4,g0)
    c: PointOnObject(g4,g2)
    c: Tangent(g0,g3) = 1.5708
    c: Tangent(g2,g3) = 1.5708
    c: Angle(g2,g0) = 1.22173
    c: Coincident(g1,g-1)
    c: Diameter(g3) = 8
    c: DistanceY(g3,g1) = 6.5
FEATURE [PartDesign::Pad] Pad071
  Direction = (0,0,1)
  Length = 13.8
  Length2 = 10
  Profile = -> Sketch099
  ReferenceAxis = -> Sketch099 [N_Axis]
  Refine = true
  Suppressed = false
  Type = 0
FEATURE [Sketcher::SketchObject] Sketch100
  ArcFitTolerance = 1e-06
  AttachmentSupport = -> [Pad071]
  ExternalGeometry = -> [Pad071]
  FullyConstrained = true
  MakeInternals = false
  MapMode = 5
  Placement = pos=(0,0,13.8) rot=(0,0,1;0rad)
  sketch-geometry (6):
    g0: LineSegment StartX=0 StartY=-11.5 StartZ=0 EndX=3.50917 EndY=-9.04285 EndZ=0
    g1: LineSegment StartX=0 StartY=-1.5 StartZ=0 EndX=3.50917 EndY=-3.95715 EndZ=0
    g2: ArcOfCircle CenterX=1.67222 CenterY=-6.5 CenterZ=0 NormalX=0 NormalY=0 NormalZ=1 AngleXU=0 Radius=3.13695 StartAngle=5.33799 EndAngle=7.22838
    g3: LineSegment StartX=0 StartY=-1.5 StartZ=0 EndX=0 EndY=-11.5 EndZ=0
    g4: LineSegment [constr] StartX=1.67222 StartY=-6.5 StartZ=0 EndX=4.80917 EndY=-6.5 EndZ=0
    g5: LineSegment [constr] StartX=4.80917 StartY=-6.5 StartZ=0 EndX=6.30917 EndY=-6.5 EndZ=0
  constraints (19):
    c: PointOnObject(g0,g-2)
    c: PointOnObject(g1,g-2)
    c: Coincident(g2,g1)
    c: Coincident(g2,g0)
    c: Coincident(g3,g1)
    c: Coincident(g3,g0)
    c: DistanceY(g-5,g0) = 1.5
    c: DistanceY(g1,g-1) = 1.5
    c: Parallel(g1,g-3)
    c: Parallel(g0,g-5)
    c: DistanceX(g1,g0) = 0
    c: Coincident(g4,g2)
    c: PointOnObject(g4,g2)
    c: Horizontal(g4)
    c: Coincident(g5,g4)
    c: PointOnObject(g5,g-4)
    c: Horizontal(g5)
    c: DistanceX(g5,g5) = 1.5
    c: DistanceX(g0,g4) = 1.3
FEATURE [PartDesign::Pocket] Pocket036
  BaseFeature = -> Pad071
  Direction = (0,0,-1)
  Length = 12.3
  Length2 = 5
  Profile = -> Sketch100
  ReferenceAxis = -> Sketch100 [N_Axis]
  Refine = true
  Suppressed = false
  Type = 0
FEATURE [Sketcher::SketchObject] Sketch101
  ArcFitTolerance = 1e-06
  AttachmentSupport = -> [Pocket036]
  ExternalGeometry = -> [Pocket036]
  FullyConstrained = true
  MakeInternals = false
  MapMode = 5
  Placement = pos=(0,0,13.8) rot=(0,0,1;0rad)
  sketch-geometry (4):
    g0: LineSegment StartX=0 StartY=-1.5 StartZ=0 EndX=0 EndY=-11.5 EndZ=0
    g1: LineSegment StartX=0 StartY=-11.5 StartZ=0 EndX=3.50917 EndY=-9.04285 EndZ=0
    g2: LineSegment StartX=0 StartY=-1.5 StartZ=0 EndX=3.50917 EndY=-3.95715 EndZ=0
    g3: ArcOfCircle CenterX=1.67222 CenterY=-6.5 CenterZ=0 NormalX=0 NormalY=0 NormalZ=1 AngleXU=0 Radius=3.13695 StartAngle=5.33799 EndAngle=7.22838
  constraints (9):
    c: Coincident(g0,g-3)
    c: Coincident(g0,g-5)
    c: Coincident(g1,g0)
    c: Coincident(g1,g-5)
    c: Coincident(g2,g0)
    c: Coincident(g2,g-4)
    c: Coincident(g3,g2)
    c: Coincident(g3,g1)
    c: Tangent(g3,g-4)
FEATURE [PartDesign::Pad] Pad072
  BaseFeature = -> Pocket036
  Direction = (0,0,1)
  Length = 1.5
  Length2 = 10
  Profile = -> Sketch101
  ReferenceAxis = -> Sketch101 [N_Axis]
  Refine = true
  Reversed = true
  Suppressed = false
  Type = 0
FEATURE [Sketcher::SketchObject] Sketch102
  ArcFitTolerance = 1e-06
  AttachmentSupport = -> [Pad072]
  ExternalGeometry = -> [Pad072]
  FullyConstrained = true
  MakeInternals = false
  MapMode = 5
  Placement = pos=(0,0,13.8) rot=(0,0,1;0rad)
  sketch-geometry (9):
    g0: LineSegment StartX=0 StartY=0 StartZ=0 EndX=-2 EndY=1.40042 EndZ=0
    g1: LineSegment StartX=-2 StartY=1.40042 StartZ=0 EndX=-2 EndY=-12.9004 EndZ=0
    g2: LineSegment StartX=-2 StartY=-12.9004 StartZ=0 EndX=-3.72022 EndY=-14.1049 EndZ=0
    g3: LineSegment StartX=-3.72022 StartY=-14.1049 StartZ=0 EndX=-1.57708 EndY=-15.1043 EndZ=0
    g4: LineSegment StartX=-1.57708 StartY=-15.1043 StartZ=0 EndX=0 EndY=-14 EndZ=0
    g5: LineSegment StartX=0 StartY=-14 StartZ=0 EndX=0 EndY=0 EndZ=0
    g6: LineSegment [constr] StartX=0 StartY=-6.59958 StartZ=0 EndX=-2 EndY=-6.59958 EndZ=0
    g7: LineSegment [constr] StartX=-2.49149 StartY=-13.2446 StartZ=0 EndX=-1.31688 EndY=-14.9221 EndZ=0
    g8: LineSegment [constr] StartX=-2 StartY=-12.9004 StartZ=0 EndX=0 EndY=-11.5 EndZ=0
  constraints (27):
    c: Coincident(g0,g-1)
    c: Coincident(g1,g0)
    c: Vertical(g1)
    c: Coincident(g2,g1)
    c: Coincident(g3,g2)
    c: Coincident(g4,g3)
    c: PointOnObject(g4,g-2)
    c: Coincident(g5,g4)
    c: Coincident(g5,g0)
    c: PointOnObject(g6,g1)
    c: Horizontal(g6)
    c: DistanceX(g6,g6) = 2
    c: DistanceY(g6,g0) = 8
    c: Angle(g0,g-3) = 3.14159
    c: Parallel(g-5,g4)
    c: Parallel(g2,g4)
    c: Angle(g3,g2) = 1.0472
    c: PointOnObject(g7,g2)
    c: PointOnObject(g7,g4)
    c: Perpendicular(g7,g2)
    c: Distance(g7,g2) = 1.5
    c: PointOnObject(g6,g5)
    c: DistanceY(g4,g-5) = 1
    c: Distance(g2) = 2.1
    c: Coincident(g8,g1)
    c: Coincident(g8,g-6)
    c: Angle(g2,g8) = 3.14159
FEATURE [PartDesign::Pad] Pad073
  BaseFeature = -> Pad072
  Direction = (0,0,1)
  Length = 1.5
  Length2 = 10
  Profile = -> Sketch102
  ReferenceAxis = -> Sketch102 [N_Axis]
  Refine = true
  Reversed = true
  Suppressed = false
  Type = 0
FEATURE [PartDesign::Pad] Pad074
  BaseFeature = -> Pad073
  Direction = (0,0,1)
  Length = 0.5
  Length2 = 10
  Profile = -> Sketch102
  ReferenceAxis = -> Sketch102 [N_Axis]
  Refine = true
  Suppressed = false
  Type = 0
FEATURE [Sketcher::SketchObject] Sketch103
  ArcFitTolerance = 1e-06
  AttachmentSupport = -> [Pad074]
  ExternalGeometry = -> [Pad074]
  FullyConstrained = true
  MakeInternals = false
  MapMode = 5
  Placement = pos=(3.4e-15,0,12.3) rot=(1,0,0;3.14159rad)
  sketch-geometry (10):
    g0: LineSegment StartX=-3.4e-15 StartY=1.5 StartZ=0 EndX=0 EndY=0 EndZ=0
    g1: LineSegment StartX=0 StartY=0 StartZ=0 EndX=-2 EndY=-1.40042 EndZ=0
    g2: LineSegment StartX=-3.4e-15 StartY=1.5 StartZ=0 EndX=-2 EndY=0.0995849 EndZ=0
    g3: LineSegment StartX=-2 StartY=0.0995849 StartZ=0 EndX=-2 EndY=-1.40042 EndZ=0
    g4: LineSegment StartX=-1.57708 StartY=15.1043 StartZ=0 EndX=-3.72022 EndY=14.1049 EndZ=0
    g5: LineSegment StartX=-3.72022 StartY=14.1049 StartZ=0 EndX=-2 EndY=12.9004 EndZ=0
    g6: LineSegment StartX=-1.57708 StartY=15.1043 StartZ=0 EndX=0 EndY=14 EndZ=0
    g7: LineSegment StartX=0 StartY=14 StartZ=0 EndX=0 EndY=13 EndZ=0
    g8: LineSegment StartX=0 StartY=11.5 StartZ=0 EndX=-2 EndY=12.9004 EndZ=0
    g9: LineSegment StartX=0 StartY=13 StartZ=0 EndX=0 EndY=11.5 EndZ=0
  constraints (21):
    c: Coincident(g0,g-4)
    c: Coincident(g0,g-1)
    c: Coincident(g1,g0)
    c: Coincident(g1,g-10)
    c: Coincident(g2,g0)
    c: PointOnObject(g2,g-10)
    c: Coincident(g3,g2)
    c: Coincident(g3,g1)
    c: Parallel(g1,g2)
    c: Coincident(g4,g-8)
    c: Coincident(g4,g-9)
    c: Coincident(g5,g4)
    c: Coincident(g5,g-10)
    c: Coincident(g6,g4)
    c: Coincident(g6,g-7)
    c: Coincident(g7,g6)
    c: Coincident(g7,g-6)
    c: Coincident(g8,g-3)
    c: Coincident(g8,g5)
    c: Coincident(g9,g7)
    c: Coincident(g9,g-3)
FEATURE [PartDesign::Pad] Pad075
  BaseFeature = -> Pad074
  Direction = (0,0,-1)
  Length = 10.8
  Length2 = 10
  Profile = -> Sketch103
  ReferenceAxis = -> Sketch103 [N_Axis]
  Refine = true
  Suppressed = false
  Type = 0
FEATURE [Sketcher::SketchObject] Sketch104
  ArcFitTolerance = 1e-06
  AttachmentSupport = -> [Pad075]
  ExternalGeometry = -> [Pad075]
  FullyConstrained = true
  MakeInternals = false
  MapMode = 5
  Placement = pos=(0,0,1.5) rot=(1,0,0;3.14159rad)
  sketch-geometry (6):
    g0: LineSegment StartX=0 StartY=14 StartZ=0 EndX=0 EndY=0 EndZ=0
    g1: LineSegment StartX=0 StartY=0 StartZ=0 EndX=-2 EndY=-1.40042 EndZ=0
    g2: LineSegment StartX=-2 StartY=-1.40042 StartZ=0 EndX=-2 EndY=12.9004 EndZ=0
    g3: LineSegment StartX=-2 StartY=12.9004 StartZ=0 EndX=-3.72022 EndY=14.1049 EndZ=0
    g4: LineSegment StartX=-3.72022 StartY=14.1049 StartZ=0 EndX=-1.57708 EndY=15.1043 EndZ=0
    g5: LineSegment StartX=-1.57708 StartY=15.1043 StartZ=0 EndX=0 EndY=14 EndZ=0
  constraints (12):
    c: Coincident(g0,g-7)
    c: Coincident(g0,g-1)
    c: Coincident(g1,g0)
    c: Coincident(g1,g-4)
    c: Coincident(g2,g1)
    c: Coincident(g2,g-3)
    c: Coincident(g3,g2)
    c: Coincident(g3,g-9)
    c: Coincident(g4,g3)
    c: Coincident(g4,g-8)
    c: Coincident(g5,g4)
    c: Coincident(g5,g0)
FEATURE [PartDesign::Pad] Pad076
  BaseFeature = -> Pad075
  Direction = (0,0,-1)
  Length = 2
  Length2 = 10
  Profile = -> Sketch104
  ReferenceAxis = -> Sketch104 [N_Axis]
  Refine = true
  Suppressed = false
  Type = 0
FEATURE [Sketcher::SketchObject] Sketch105
  ArcFitTolerance = 1e-06
  AttachmentSupport = -> [Pad076]
  ExternalGeometry = -> [Pad076]
  FullyConstrained = true
  MakeInternals = false
  MapMode = 5
  Placement = pos=(5.40323,-7.71662,-2.01e-14) rot=(-0.217607,0.690162,0.690162;3.57013rad)
  sketch-geometry (17):
    g0: LineSegment [constr] StartX=9.03768 StartY=12.3 StartZ=0 EndX=9.03768 EndY=1.5 EndZ=0
    g1: LineSegment StartX=11.1377 StartY=12.6 StartZ=0 EndX=9.03768 EndY=12.6 EndZ=0
    g2: LineSegment StartX=9.03768 StartY=12.6 StartZ=0 EndX=9.03768 EndY=11.025 EndZ=0
    g3: LineSegment StartX=9.03768 StartY=11.025 StartZ=0 EndX=11.1377 EndY=11.025 EndZ=0
    g4: LineSegment StartX=11.1377 StartY=11.025 StartZ=0 EndX=11.1377 EndY=12.6 EndZ=0
    g5: LineSegment StartX=11.1377 StartY=9.325 StartZ=0 EndX=9.03768 EndY=9.325 EndZ=0
    g6: LineSegment StartX=9.03768 StartY=9.325 StartZ=0 EndX=9.03768 EndY=7.75 EndZ=0
    g7: LineSegment StartX=9.03768 StartY=7.75 StartZ=0 EndX=11.1377 EndY=7.75 EndZ=0
    g8: LineSegment StartX=11.1377 StartY=7.75 StartZ=0 EndX=11.1377 EndY=9.325 EndZ=0
    g9: LineSegment StartX=11.1377 StartY=6.05 StartZ=0 EndX=9.03768 EndY=6.05 EndZ=0
    g10: LineSegment StartX=9.03768 StartY=6.05 StartZ=0 EndX=9.03768 EndY=4.475 EndZ=0
    g11: LineSegment StartX=9.03768 StartY=4.475 StartZ=0 EndX=11.1377 EndY=4.475 EndZ=0
    g12: LineSegment StartX=11.1377 StartY=4.475 StartZ=0 EndX=11.1377 EndY=6.05 EndZ=0
    g13: LineSegment StartX=11.1377 StartY=2.775 StartZ=0 EndX=9.03768 EndY=2.775 EndZ=0
    g14: LineSegment StartX=9.03768 StartY=2.775 StartZ=0 EndX=9.03768 EndY=1.2 EndZ=0
    g15: LineSegment StartX=9.03768 StartY=1.2 StartZ=0 EndX=11.1377 EndY=1.2 EndZ=0
    g16: LineSegment StartX=11.1377 StartY=1.2 StartZ=0 EndX=11.1377 EndY=2.775 EndZ=0
  constraints (51):
    c: Coincident(g0,g-4)
    c: Coincident(g0,g-5)
    c: Coincident(g1,g2)
    c: Coincident(g2,g3)
    c: Coincident(g3,g4)
    c: Coincident(g4,g1)
    c: Horizontal(g1)
    c: Horizontal(g3)
    c: Vertical(g2)
    c: Vertical(g4)
    c: PointOnObject(g1,g-3)
    c: PointOnObject(g2,g0)
    c: Coincident(g5,g6)
    c: Coincident(g6,g7)
    c: Coincident(g7,g8)
    c: Coincident(g8,g5)
    c: Horizontal(g5)
    c: Horizontal(g7)
    c: Vertical(g6)
    c: Vertical(g8)
    c: PointOnObject(g5,g-3)
    c: Coincident(g9,g10)
    c: Coincident(g10,g11)
    c: Coincident(g11,g12)
    c: Coincident(g12,g9)
    c: Horizontal(g9)
    c: Horizontal(g11)
    c: Vertical(g10)
    c: Vertical(g12)
    c: PointOnObject(g9,g-3)
    c: PointOnObject(g10,g0)
    c: Coincident(g13,g14)
    c: Coincident(g14,g15)
    c: Coincident(g15,g16)
    c: Coincident(g16,g13)
    c: Horizontal(g13)
    c: Horizontal(g15)
    c: Vertical(g14)
    c: Vertical(g16)
    c: PointOnObject(g13,g-3)
    c: PointOnObject(g14,g0)
    c: DistanceY(g1,g-3) = 1.7
    c: DistanceY(g5,g3) = 1.7
    c: DistanceY(g9,g7) = 1.7
    c: DistanceY(g13,g11) = 1.7
    c: DistanceY(g-3,g15) = 1.7
    c: DistanceY(g-3,g-3) = 14.8
    c: DistanceY(g4,g4) = 1.575
    c: DistanceY(g8,g8) = 1.575
    c: DistanceY(g12,g12) = 1.575
    c: PointOnObject(g6,g0)
FEATURE [PartDesign::Pocket] Pocket037
  BaseFeature = -> Pad076
  Direction = (0.573576,-0.819152,-2.2e-15)
  Length = 5
  Length2 = 5
  Profile = -> Sketch105
  ReferenceAxis = -> Sketch105 [N_Axis]
  Refine = true
  Suppressed = false
  Type = 0
FEATURE [Sketcher::SketchObject] Sketch106
  ArcFitTolerance = 1e-06
  AttachmentOffset = pos=(0,0,-5.65) rot=(0,0,1;0rad)
  AttachmentSupport = -> [Pocket037]
  ExternalGeometry = -> [Pocket037]
  FullyConstrained = true
  MakeInternals = false
  MapMode = 5
  Placement = pos=(3.2e-15,0,8.15) rot=(0,0,1;0rad)
  sketch-geometry (4):
    g0: LineSegment StartX=0 StartY=0 StartZ=0 EndX=4.58725 EndY=-3.21203 EndZ=0
    g1: LineSegment StartX=4.58725 StartY=-3.21203 StartZ=0 EndX=4.58725 EndY=0.287972 EndZ=0
    g2: LineSegment StartX=0 StartY=0 StartZ=0 EndX=2.04788 EndY=1.43394 EndZ=0
    g3: ArcOfCircle CenterX=2.99379 CenterY=0.143492 CenterZ=0 NormalX=0 NormalY=0 NormalZ=1 AngleXU=0 Radius=1.6 StartAngle=0.090423 EndAngle=2.20333
  constraints (12):
    c: Coincident(g0,g-1)
    c: PointOnObject(g0,g-3)
    c: Coincident(g1,g0)
    c: Vertical(g1)
    c: Coincident(g2,g0)
    c: Coincident(g3,g2)
    c: Coincident(g3,g1)
    c: Distance(g0) = 5.6
    c: Parallel(g2,g-4)
    c: DistanceY(g1,g1) = 3.5
    c: Distance(g2) = 2.5
    c: Radius(g3) = 1.6
FEATURE [PartDesign::Pad] Pad077
  BaseFeature = -> Pocket037
  Direction = (0,0,1)
  Length = 2.5
  Length2 = 10
  Profile = -> Sketch106
  ReferenceAxis = -> Sketch106 [N_Axis]
  Refine = true
  Reversed = true
  Suppressed = false
  Type = 0
FEATURE [Sketcher::SketchObject] Sketch107
  ArcFitTolerance = 1e-06
  AttachmentOffset = pos=(0,0,-0.25) rot=(0,0,1;0rad)
  AttachmentSupport = -> [Pad077]
  ExternalGeometry = -> [Pad077]
  FullyConstrained = true
  MakeInternals = false
  MapMode = 5
  Placement = pos=(0,0,7.9) rot=(0,0,1;0rad)
  sketch-geometry (7):
    g0: LineSegment StartX=-2 StartY=1.40042 StartZ=0 EndX=-14.65 EndY=23.3109 EndZ=0
    g1: LineSegment StartX=1.02951 StartY=0.720867 StartZ=0 EndX=-10.2333 EndY=25.8609 EndZ=0
    g2: LineSegment StartX=1.02951 StartY=0.720867 StartZ=0 EndX=0 EndY=3e-16 EndZ=0
    g3: LineSegment StartX=0 StartY=3e-16 StartZ=0 EndX=-2 EndY=1.40042 EndZ=0
    g4: LineSegment [constr] StartX=-2 StartY=1.40042 StartZ=0 EndX=0.165064 EndY=2.65042 EndZ=0
    g5: LineSegment [constr] StartX=-14.65 StartY=23.3109 StartZ=0 EndX=-10.2333 EndY=25.8609 EndZ=0
    g6: LineSegment StartX=-14.65 StartY=23.3109 StartZ=0 EndX=-10.2333 EndY=25.8609 EndZ=0
  constraints (18):
    c: Coincident(g0,g-3)
    c: PointOnObject(g1,g-4)
    c: Coincident(g2,g1)
    c: Coincident(g2,g-1)
    c: Coincident(g3,g2)
    c: Coincident(g3,g0)
    c: Distance(g0) = 25.3
    c: Coincident(g4,g0)
    c: PointOnObject(g4,g1)
    c: Perpendicular(g0,g4)
    c: Distance(g4) = 2.5
    c: Coincident(g5,g0)
    c: Perpendicular(g0,g5)
    c: Distance(g5) = 5.1
    c: Coincident(g1,g5)
    c: Coincident(g6,g0)
    c: Coincident(g6,g1)
    c: Angle(g0,g-5) = 2.61799
FEATURE [PartDesign::Pad] Pad078
  BaseFeature = -> Pad077
  Direction = (0,0,1)
  Length = 2
  Length2 = 10
  Profile = -> Sketch107
  ReferenceAxis = -> Sketch107 [N_Axis]
  Refine = true
  Reversed = true
  Suppressed = false
  Type = 0
FEATURE [Sketcher::SketchObject] Sketch108
  ArcFitTolerance = 1e-06
  AttachmentSupport = -> [Pad078]
  ExternalGeometry = -> [Pad078]
  FullyConstrained = false
  MakeInternals = false
  MapMode = 5
  Placement = pos=(0,0,7.9) rot=(0,0,1;0rad)
  sketch-geometry (14):
    g0: ArcOfCircle CenterX=-16.15 CenterY=25.9089 CenterZ=0 NormalX=0 NormalY=0 NormalZ=1 AngleXU=0 Radius=3 StartAngle=2.0944 EndAngle=5.23599
    g1: LineSegment [constr] StartX=-17.65 StartY=28.507 StartZ=0 EndX=-16.15 EndY=25.9089 EndZ=0
    g2: LineSegment [constr] StartX=-16.15 StartY=25.9089 StartZ=0 EndX=-14.65 EndY=23.3109 EndZ=0
    g3: LineSegment StartX=-17.65 StartY=28.507 StartZ=0 EndX=-19.6 EndY=31.8845 EndZ=0
    g4: ArcOfCircle CenterX=-18.734 CenterY=32.3845 CenterZ=0 NormalX=0 NormalY=0 NormalZ=1 AngleXU=0 Radius=1 StartAngle=0.872665 EndAngle=3.66519
    g5: LineSegment StartX=-18.0912 StartY=33.1506 StartZ=0 EndX=-15.7164 EndY=31.1579 EndZ=0
    g6: LineSegment StartX=-15.7164 StartY=31.1579 StartZ=0 EndX=-14.8504 EndY=31.6579 EndZ=0
    g7: LineSegment StartX=-14.8504 StartY=31.6579 StartZ=0 EndX=-11.4663 EndY=28.6131 EndZ=0
    g8: LineSegment StartX=-11.4663 StartY=28.6131 StartZ=0 EndX=-10.2333 EndY=25.8609 EndZ=0
    g9: LineSegment [constr] StartX=-19.6 StartY=31.8845 StartZ=0 EndX=-18.734 EndY=32.3845 EndZ=0
    g10: LineSegment [constr] StartX=-11.4663 StartY=28.6131 StartZ=0 EndX=-16.15 EndY=25.9089 EndZ=0
    g11: LineSegment [constr] StartX=-18.734 StartY=32.3845 StartZ=0 EndX=-18.0912 EndY=33.1506 EndZ=0
    g12: LineSegment [constr] StartX=-15.7164 StartY=31.1579 StartZ=0 EndX=-18.3145 EndY=29.6579 EndZ=0
    g13: LineSegment StartX=-10.2333 StartY=25.8609 StartZ=0 EndX=-14.65 EndY=23.3109 EndZ=0
  constraints (36):
    c: Coincident(g0,g-3)
    c: Radius(g0) = 3
    c: Coincident(g1,g0)
    c: Coincident(g1,g0)
    c: Coincident(g2,g0)
    c: Coincident(g2,g0)
    c: Angle(g1,g2) = 3.14159
    c: Angle(g-4,g2) = 3.14159
    c: Coincident(g3,g0)
    c: Angle(g3,g1) = 3.14159
    c: Coincident(g4,g3)
    c: Coincident(g5,g4)
    c: Coincident(g6,g5)
    c: Coincident(g7,g6)
    c: Coincident(g8,g7)
    c: Coincident(g8,g-5)
    c: Angle(g-5,g8) = 3.14159
    c: Radius(g4) = 1
    c: Distance(g0,g3) = 3.9
    c: Coincident(g9,g3)
    c: Coincident(g9,g4)
    c: Perpendicular(g3,g9)
    c: Coincident(g10,g7)
    c: Coincident(g10,g0)
    c: Perpendicular(g10,g2)
    c: Distance(g5) = 3.1
    c: Coincident(g11,g4)
    c: Coincident(g11,g4)
    c: Angle(g11,g9) = 2.79253
    c: Coincident(g12,g5)
    c: PointOnObject(g12,g3)
    c: Perpendicular(g3,g12)
    c: Distance(g12) = 3
    c: Angle(g12,g6) = 3.14159
    c: Coincident(g13,g0)
    c: Coincident(g13,g8)
FEATURE [PartDesign::Pad] Pad079
  BaseFeature = -> Pad078
  Direction = (0,0,1)
  Length = 2
  Length2 = 10
  Profile = -> Sketch108
  ReferenceAxis = -> Sketch108 [N_Axis]
  Refine = true
  Reversed = true
  Suppressed = false
  Type = 0
FEATURE [Sketcher::SketchObject] Sketch109
  ArcFitTolerance = 1e-06
  AttachmentSupport = -> [Pad079]
  ExternalGeometry = -> [Pad079]
  FullyConstrained = true
  MakeInternals = false
  MapMode = 5
  Placement = pos=(0,0,7.9) rot=(0,0,1;0rad)
  sketch-geometry (1):
    g0: Circle CenterX=-16.15 CenterY=25.9089 CenterZ=0 NormalX=0 NormalY=0 NormalZ=1 AngleXU=0 Radius=0.75
  constraints (2):
    c: Coincident(g0,g-3)
    c: Radius(g0) = 0.75
FEATURE [PartDesign::Pocket] Pocket038
  BaseFeature = -> Pad079
  Direction = (0,0,-1)
  Length = 5
  Length2 = 5
  Profile = -> Sketch109
  ReferenceAxis = -> Sketch109 [N_Axis]
  Refine = true
  Suppressed = false
  Type = 0
FEATURE [Sketcher::SketchObject] Sketch110
  ArcFitTolerance = 1e-06
  AttachmentSupport = -> [Pocket038]
  ExternalGeometry = -> [Pocket038]
  FullyConstrained = true
  MakeInternals = false
  MapMode = 5
  Placement = pos=(0,0,8.15) rot=(0,0,1;0rad)
  sketch-geometry (1):
    g0: Circle CenterX=2.99379 CenterY=0.143492 CenterZ=0 NormalX=0 NormalY=0 NormalZ=1 AngleXU=0 Radius=0.95
  constraints (2):
    c: Coincident(g0,g-3)
    c: Diameter(g0) = 1.9
FEATURE [PartDesign::Pad] Pad080
  BaseFeature = -> Pocket038
  Direction = (0,0,1)
  Length = 0.3
  Length2 = 10
  Profile = -> Sketch110
  ReferenceAxis = -> Sketch110 [N_Axis]
  Refine = true
  Suppressed = false
  Type = 0
FEATURE [Sketcher::SketchObject] Sketch111
  ArcFitTolerance = 1e-06
  AttachmentSupport = -> [Pad080]
  ExternalGeometry = -> [Pad080]
  FullyConstrained = true
  MakeInternals = false
  MapMode = 5
  Placement = pos=(0,0,5.65) rot=(1,0,0;3.14159rad)
  sketch-geometry (1):
    g0: Circle CenterX=2.99379 CenterY=-0.143492 CenterZ=0 NormalX=0 NormalY=0 NormalZ=1 AngleXU=0 Radius=0.95
  constraints (2):
    c: Coincident(g0,g-3)
    c: Diameter(g0) = 1.9
FEATURE [PartDesign::Pad] Pad081
  BaseFeature = -> Pad080
  Direction = (0,0,-1)
  Length = 0.3
  Length2 = 10
  Profile = -> Sketch111
  ReferenceAxis = -> Sketch111 [N_Axis]
  Refine = true
  Suppressed = false
  Type = 0
FEATURE [Sketcher::SketchObject] Sketch112
  ArcFitTolerance = 1e-06
  AttachmentSupport = -> [Pad081]
  ExternalGeometry = -> [Pad081]
  FullyConstrained = true
  MakeInternals = false
  MapMode = 5
  Placement = pos=(0,0,7.9) rot=(0,0,1;0rad)
  sketch-geometry (7):
    g0: LineSegment [constr] StartX=-14.65 StartY=23.3109 StartZ=0 EndX=-10.2333 EndY=25.8609 EndZ=0
    g1: LineSegment StartX=-10.2333 StartY=25.8609 StartZ=0 EndX=-7.65753 EndY=20.1115 EndZ=0
    g2: LineSegment StartX=-7.65753 StartY=20.1115 StartZ=0 EndX=-5.39731 EndY=21.4164 EndZ=0
    g3: LineSegment StartX=-10.2333 StartY=25.8609 StartZ=0 EndX=-5.61764 EndY=24.1188 EndZ=0
    g4: ArcOfCircle CenterX=-6.14731 CenterY=22.7154 CenterZ=0 NormalX=0 NormalY=0 NormalZ=1 AngleXU=0 Radius=1.5 StartAngle=5.23599 EndAngle=7.49309
    g5: GeomPoint [constr] X=-2.65399 Y=23.0003 Z=0
    g6: LineSegment [constr] StartX=-5.61764 StartY=24.1188 StartZ=0 EndX=-8.81175 EndY=22.6878 EndZ=0
  constraints (18):
    c: Coincident(g0,g-4)
    c: PointOnObject(g0,g-5)
    c: Perpendicular(g-3,g0)
    c: Coincident(g1,g0)
    c: PointOnObject(g1,g-5)
    c: Coincident(g2,g1)
    c: Coincident(g3,g0)
    c: PointOnObject(g5,g2)
    c: PointOnObject(g5,g3)
    c: Tangent(g2,g4) = -1.5708
    c: Tangent(g3,g4) = 1.5708
    c: Distance(g1) = 6.3
    c: Coincident(g6,g3)
    c: PointOnObject(g6,g1)
    c: Perpendicular(g1,g6)
    c: Distance(g6) = 3.5
    c: Radius(g4) = 1.5
    c: Perpendicular(g-3,g2)
FEATURE [PartDesign::Pad] Pad082
  BaseFeature = -> Pad081
  Direction = (0,0,1)
  Length = 2
  Length2 = 10
  Profile = -> Sketch112
  ReferenceAxis = -> Sketch112 [N_Axis]
  Refine = true
  Reversed = true
  Suppressed = false
  Type = 0
FEATURE [Sketcher::SketchObject] Sketch113
  ArcFitTolerance = 1e-06
  AttachmentSupport = -> [Pad082]
  ExternalGeometry = -> [Pad082]
  FullyConstrained = true
  MakeInternals = false
  MapMode = 5
  Placement = pos=(0,0,7.9) rot=(0,0,1;0rad)
  sketch-geometry (1):
    g0: Circle CenterX=-6.14731 CenterY=22.7154 CenterZ=0 NormalX=0 NormalY=0 NormalZ=1 AngleXU=0 Radius=1
  constraints (2):
    c: Coincident(g0,g-3)
    c: Radius(g0) = 1
FEATURE [PartDesign::Pad] Pad083
  BaseFeature = -> Pad082
  Direction = (0,0,1)
  Length = 0.3
  Length2 = 10
  Profile = -> Sketch113
  ReferenceAxis = -> Sketch113 [N_Axis]
  Refine = true
  Suppressed = false
  Type = 0
FEATURE [Sketcher::SketchObject] Sketch114
  ArcFitTolerance = 1e-06
  AttachmentSupport = -> [Pad083]
  ExternalGeometry = -> [Pad083]
  FullyConstrained = true
  MakeInternals = false
  MapMode = 5
  Placement = pos=(0,0,5.9) rot=(1,0,0;3.14159rad)
  sketch-geometry (1):
    g0: Circle CenterX=-6.14731 CenterY=-22.7154 CenterZ=0 NormalX=0 NormalY=0 NormalZ=1 AngleXU=0 Radius=1
  constraints (2):
    c: Coincident(g0,g-3)
    c: Radius(g0) = 1
FEATURE [PartDesign::Pad] Pad084
  BaseFeature = -> Pad083
  Direction = (0,0,-1)
  Length = 0.3
  Length2 = 10
  Profile = -> Sketch114
  ReferenceAxis = -> Sketch114 [N_Axis]
  Refine = true
  Suppressed = false
  Type = 0
FEATURE [Sketcher::SketchObject] Sketch115
  ArcFitTolerance = 1e-06
  AttachmentSupport = -> [Pad084]
  ExternalGeometry = -> [Pad084]
  FullyConstrained = true
  MakeInternals = false
  MapMode = 5
  Placement = pos=(0,0,7.9) rot=(0,0,1;0rad)
  sketch-geometry (6):
    g0: LineSegment [constr] StartX=-5.39731 StartY=21.4164 StartZ=0 EndX=3.62894 EndY=5.78247 EndZ=0
    g1: LineSegment [constr] StartX=3.62894 StartY=5.78247 StartZ=0 EndX=2.99379 EndY=0.143492 EndZ=0
    g2: Circle CenterX=-1.36442 CenterY=2.89955 CenterZ=0 NormalX=0 NormalY=0 NormalZ=1 AngleXU=0 Radius=1
    g3: LineSegment [constr] StartX=-1.36442 StartY=2.89955 StartZ=0 EndX=-2.49025 EndY=2.24955 EndZ=0
    g4: LineSegment [constr] StartX=-1.36442 StartY=2.89955 StartZ=0 EndX=-0.237924 EndY=3.54994 EndZ=0
    g5: LineSegment [constr] StartX=-0.237924 StartY=3.54994 StartZ=0 EndX=3.62894 EndY=5.78247 EndZ=0
  constraints (17):
    c: Coincident(g0,g-3)
    c: Perpendicular(g-4,g0)
    c: Coincident(g1,g0)
    c: Coincident(g1,g-6)
    c: Radius(g2) = 1
    c: Coincident(g3,g2)
    c: PointOnObject(g3,g-8)
    c: Coincident(g4,g2)
    c: PointOnObject(g4,g-7)
    c: Angle(g4,g3) = 3.14159
    c: Perpendicular(g-8,g3)
    c: Distance(g4,g-7) = 3.1
    c: Distance(g3,g4) = 2.60076
    c: Distance(g3,g2) = 1.3
    c: Coincident(g5,g4)
    c: Coincident(g5,g0)
    c: Perpendicular(g5,g0)
FEATURE [PartDesign::Pad] Pad085
  BaseFeature = -> Pad084
  Direction = (0,0,1)
  Length = 0.3
  Length2 = 10
  Profile = -> Sketch115
  ReferenceAxis = -> Sketch115 [N_Axis]
  Refine = true
  Suppressed = false
  Type = 0
FEATURE [Sketcher::SketchObject] Sketch116
  ArcFitTolerance = 1e-06
  AttachmentSupport = -> [Pad085]
  ExternalGeometry = -> [Pad085]
  FullyConstrained = true
  MakeInternals = false
  MapMode = 5
  Placement = pos=(0,0,5.9) rot=(1,0,0;3.14159rad)
  sketch-geometry (1):
    g0: Circle CenterX=-1.36442 CenterY=-2.89955 CenterZ=0 NormalX=0 NormalY=0 NormalZ=1 AngleXU=0 Radius=1
  constraints (2):
    c: Coincident(g0,g-3)
    c: Equal(g0,g-3)
FEATURE [PartDesign::Pad] Pad086
  BaseFeature = -> Pad085
  Direction = (0,0,-1)
  Length = 0.3
  Length2 = 10
  Profile = -> Sketch116
  ReferenceAxis = -> Sketch116 [N_Axis]
  Refine = true
  Suppressed = false
  Type = 0
FEATURE [Sketcher::SketchObject] Sketch117
  ArcFitTolerance = 1e-06
  AttachmentSupport = -> [Pad086]
  ExternalGeometry = -> [Pad086]
  FullyConstrained = true
  MakeInternals = false
  MapMode = 5
  Placement = pos=(-10.6229,18.3994,0) rot=(0.935113,0.250563,0.250563;1.63783rad)
  sketch-geometry (1):
    g0: Circle CenterX=6.03399 CenterY=6.9 CenterZ=0 NormalX=0 NormalY=0 NormalZ=1 AngleXU=0 Radius=1.3
  constraints (2):
    c: Symmetric(g-3,g-3,g0)
    c: Diameter(g0) = 2.6
FEATURE [PartDesign::Pad] Pad087
  BaseFeature = -> Pad086
  Direction = (0.5,-0.866025,2e-16)
  Length = 10
  Length2 = 10
  Profile = -> Sketch117
  ReferenceAxis = -> Sketch117 [N_Axis]
  Refine = true
  Suppressed = false
  Type = 0
FEATURE [Sketcher::SketchObject] Sketch118
  ArcFitTolerance = 1e-06
  AttachmentSupport = -> [Pad087]
  ExternalGeometry = -> [Pad087]
  FullyConstrained = true
  MakeInternals = false
  MapMode = 5
  Placement = pos=(-5.6229,9.73915,2.2e-15) rot=(0.935113,0.250563,0.250563;1.63783rad)
  sketch-geometry (4):
    g0: LineSegment StartX=4.03399 StartY=8.75 StartZ=0 EndX=4.03399 EndY=5.05 EndZ=0
    g1: LineSegment StartX=4.03399 StartY=5.05 StartZ=0 EndX=8.03399 EndY=5.05 EndZ=0
    g2: LineSegment StartX=8.03399 StartY=5.05 StartZ=0 EndX=8.03399 EndY=8.75 EndZ=0
    g3: LineSegment StartX=8.03399 StartY=8.75 StartZ=0 EndX=4.03399 EndY=8.75 EndZ=0
  constraints (12):
    c: Coincident(g0,g1)
    c: Coincident(g1,g2)
    c: Coincident(g2,g3)
    c: Coincident(g3,g0)
    c: Vertical(g0)
    c: Vertical(g2)
    c: Horizontal(g1)
    c: Horizontal(g3)
    c: DistanceX(g3,g3) = 4
    c: DistanceY(g2,g2) = 3.7
    c: DistanceY(g-3,g2) = 1.85
    c: DistanceX(g0,g-3) = 2
FEATURE [PartDesign::Pad] Pad088
  BaseFeature = -> Pad087
  Direction = (0.5,-0.866025,0)
  Length = 1
  Length2 = 10
  Profile = -> Sketch118
  ReferenceAxis = -> Sketch118 [N_Axis]
  Refine = true
  Suppressed = false
  Type = 0
FEATURE [Sketcher::SketchObject] Sketch119
  ArcFitTolerance = 1e-06
  AttachmentSupport = -> [Pad088]
  ExternalGeometry = -> [Pad088]
  FullyConstrained = true
  MakeInternals = false
  MapMode = 5
  Placement = pos=(-5.1229,8.87312,2.5e-15) rot=(0.935113,0.250563,0.250563;1.63783rad)
  sketch-geometry (1):
    g0: Circle CenterX=6.03399 CenterY=6.9 CenterZ=0 NormalX=0 NormalY=0 NormalZ=1 AngleXU=0 Radius=1.3
  constraints (2):
    c: Coincident(g0,g-3)
    c: Equal(g0,g-3)
FEATURE [PartDesign::Pad] Pad089
  BaseFeature = -> Pad088
  Direction = (0.5,-0.866025,2e-16)
  Length = 1
  Length2 = 10
  Profile = -> Sketch119
  ReferenceAxis = -> Sketch119 [N_Axis]
  Refine = true
  Suppressed = false
  Type = 0
FEATURE [Sketcher::SketchObject] Sketch120
  ArcFitTolerance = 1e-06
  AttachmentSupport = -> [Pad089]
  ExternalGeometry = -> [Pad089]
  FullyConstrained = true
  MakeInternals = false
  MapMode = 5
  Placement = pos=(1.12638,0.504623,0) rot=(0.416434,0.642878,0.642878;2.35241rad)
  sketch-geometry (1):
    g0: Circle CenterX=3.20398 CenterY=6.9 CenterZ=0 NormalX=0 NormalY=0 NormalZ=1 AngleXU=0 Radius=0.75
  constraints (5):
    c: Diameter(g0) = 1.5
    c: DistanceX(g-3,g-3) = 2
    c: DistanceY(g-4,g-3) = 2.6
    c: DistanceY(g0,g-3) = 1.3
    c: DistanceX(g-3,g0) = 1
FEATURE [PartDesign::Pad] Pad090
  BaseFeature = -> Pad089
  Direction = (0.912602,0.408848,2e-16)
  Length = 4
  Length2 = 10
  Profile = -> Sketch120
  ReferenceAxis = -> Sketch120 [N_Axis]
  Refine = true
  Suppressed = false
  Type = 0
FEATURE [Sketcher::SketchObject] Sketch121
  ArcFitTolerance = 1e-06
  AttachmentSupport = -> [Pad090]
  ExternalGeometry = -> [Pad090]
  FullyConstrained = true
  MakeInternals = false
  MapMode = 5
  Placement = pos=(0,0,8.2) rot=(0,0,1;0rad)
  sketch-geometry (3):
    g0: LineSegment [constr] StartX=0.602691 StartY=11.0241 StartZ=0 EndX=3.92521 EndY=5.26932 EndZ=0
    g1: LineSegment [constr] StartX=3.46685 StartY=5.06397 StartZ=0 EndX=3.92521 EndY=5.26932 EndZ=0
    g2: Circle CenterX=3.92521 CenterY=5.26932 CenterZ=0 NormalX=0 NormalY=0 NormalZ=1 AngleXU=0 Radius=1
  constraints (7):
    c: Symmetric(g-3,g-3,g0)
    c: Perpendicular(g0,g-3)
    c: Symmetric(g-4,g-4,g1)
    c: Coincident(g1,g0)
    c: Perpendicular(g-4,g1)
    c: Coincident(g2,g0)
    c: Radius(g2) = 1
FEATURE [PartDesign::Body] Body004  label="Upper_Scoop"
  AllowCompound = false
  Group = -> [Sketch099,Pad071,Sketch100,Pocket036,Sketch101,Pad072,Sketch102,Pad073,Pad074,Sketch103,Pad075,Sketch104,Pad076,Sketch105,Pocket037,Sketch106,Pad077,Sketch107,Pad078,Sketch108,Pad079,Sketch109,Pocket038,Sketch110,Pad080,Sketch111,Pad081,Sketch112,Pad082,Sketch113,Pad083,Sketch114,Pad084,Sketch115,Pad085,Sketch116,Pad086,Sketch117,Pad087,Sketch118,Pad088,Sketch119,Pad089,Sketch120,Pad090,Sketch121,+28 more]
  Origin = -> Origin004
  Placement = pos=(96.4151,-9.45,10.8146) rot=(0.981945,-0.132962,0.134557;1.5851rad)
  Tip = -> Fillet009
COMPONENT P5 — recipe-attached ("Chest_Plate", modeled in this document).
Construction recipe (the document's own serialized feature program — sketch geometry with constraints, then the solid features built on it; lengths are millimeters unless a unit is written):

FEATURE [PartDesign::SubShapeBinder] Binder002
  BindCopyOnChange = 0
  BindMode = 2
  ClaimChildren = false
  Context = -> Body005 [Binder002.]
  Fuse = false
  MakeFace = true
  OffsetFill = false
  OffsetIntersection = false
  OffsetJoinType = 0
  OffsetOpenResult = false
  PartialLoad = false
  Refine = true
  Relative = true
  _Version = 2
FEATURE [Sketcher::SketchObject] Sketch133
  ArcFitTolerance = 1e-06
  AttachmentSupport = -> [Binder002]
  ExternalGeometry = -> [Binder002]
  FullyConstrained = true
  MakeInternals = false
  MapMode = 5
  Placement = pos=(0,0,-10.2) rot=(1,0,0;3.14159rad)
  sketch-geometry (4):
    g0: LineSegment StartX=50.6 StartY=6 StartZ=0 EndX=20.6 EndY=6 EndZ=0
    g1: LineSegment StartX=50.6 StartY=26 StartZ=0 EndX=20.6 EndY=26 EndZ=0
    g2: ArcOfCircle CenterX=20.6 CenterY=16 CenterZ=0 NormalX=0 NormalY=0 NormalZ=1 AngleXU=0 Radius=10 StartAngle=1.57079 EndAngle=4.71239
    g3: LineSegment StartX=50.6 StartY=26 StartZ=0 EndX=50.6 EndY=6 EndZ=0
  constraints (14):
    c: Horizontal(g0)
    c: Horizontal(g1)
    c: Coincident(g2,g0)
    c: Coincident(g2,g1)
    c: DistanceX(g1,g0) = 0
    c: PointOnObject(g-19,g1)
    c: PointOnObject(g-13,g0)
    c: DistanceY(g-13,g-19) = 20
    c: Diameter(g2) = 20
    c: DistanceX(g0,g0) = 30
    c: DistanceX(g1,g1) = 30
    c: Coincident(g3,g1)
    c: Coincident(g3,g0)
    c: DistanceX(g-3,g2) = 0
FEATURE [PartDesign::Pad] Pad102
  Direction = (0,0,-1)
  Length = 3
  Length2 = 10
  Profile = -> Sketch133
  ReferenceAxis = -> Sketch133 [N_Axis]
  Refine = true
  Suppressed = false
  Type = 0
FEATURE [Sketcher::SketchObject] Sketch134
  ArcFitTolerance = 1e-06
  AttachmentSupport = -> [Pad102]
  ExternalGeometry = -> [Pad102]
  FullyConstrained = true
  MakeInternals = false
  MapMode = 5
  Placement = pos=(0,0,-13.2) rot=(1,0,0;3.14159rad)
  sketch-geometry (3):
    g0: Circle CenterX=20.6 CenterY=16.25 CenterZ=0 NormalX=0 NormalY=0 NormalZ=1 AngleXU=0 Radius=3.5
    g1: LineSegment [constr] StartX=20.6 StartY=26 StartZ=0 EndX=20.6 EndY=16.25 EndZ=0
    g2: LineSegment [constr] StartX=20.6 StartY=16.25 StartZ=0 EndX=20.6 EndY=6 EndZ=0
  constraints (8):
    c: Diameter(g0) = 7
    c: Coincident(g1,g-3)
    c: Coincident(g1,g0)
    c: Coincident(g2,g0)
    c: Coincident(g2,g-4)
    c: Vertical(g1)
    c: DistanceY(g0,g1) = 9.75
    c: DistanceY(g2,g1) = 20
FEATURE [PartDesign::Pocket] Pocket043
  BaseFeature = -> Pad102
  Direction = (0,0,1)
  Length = 5
  Length2 = 5
  Profile = -> Sketch134
  ReferenceAxis = -> Sketch134 [N_Axis]
  Refine = true
  Suppressed = false
  Type = 0
FEATURE [Sketcher::SketchObject] Sketch135
  ArcFitTolerance = 1e-06
  AttachmentSupport = -> [Pocket043]
  ExternalGeometry = -> [Pocket043]
  FullyConstrained = true
  MakeInternals = false
  MapMode = 5
  Placement = pos=(0,0,-10.2) rot=(0,0,1;0rad)
  sketch-geometry (2):
    g0: Circle CenterX=20.6 CenterY=-16.25 CenterZ=0 NormalX=0 NormalY=0 NormalZ=1 AngleXU=0 Radius=5
    g1: Circle CenterX=20.6 CenterY=-16.25 CenterZ=0 NormalX=0 NormalY=0 NormalZ=1 AngleXU=0 Radius=3.49999
  constraints (4):
    c: Coincident(g0,g-3)
    c: Diameter(g0) = 10
    c: Coincident(g1,g0)
    c: Tangent(g1,g-3)
FEATURE [PartDesign::Pad] Pad103
  BaseFeature = -> Pocket043
  Direction = (0,0,1)
  Length = 7.65
  Length2 = 10
  Profile = -> Sketch135
  ReferenceAxis = -> Sketch135 [N_Axis]
  Refine = true
  Suppressed = false
  Type = 0
FEATURE [Sketcher::SketchObject] Sketch136
  ArcFitTolerance = 1e-06
  AttachmentSupport = -> [Pad103]
  ExternalGeometry = -> [Pad103]
  FullyConstrained = true
  MakeInternals = false
  MapMode = 5
  Placement = pos=(0,0,-13.2) rot=(1,0,0;3.14159rad)
  sketch-geometry (1):
    g0: Circle CenterX=20.6 CenterY=16.25 CenterZ=0 NormalX=0 NormalY=0 NormalZ=1 AngleXU=0 Radius=3.55
  constraints (3):
    c: Coincident(g0,g-3)
    c: Radius(g-3) = 3.5
    c: Radius(g0) = 3.55
FEATURE [PartDesign::Pocket] Pocket044
  BaseFeature = -> Pad103
  Direction = (0,0,1)
  Length = 12
  Length2 = 5
  Profile = -> Sketch136
  ReferenceAxis = -> Sketch136 [N_Axis]
  Refine = true
  Suppressed = false
  Type = 0
FEATURE [Sketcher::SketchObject] Sketch137
  ArcFitTolerance = 1e-06
  AttachmentOffset = pos=(0,0,-6.4) rot=(0,0,1;0rad)
  AttachmentSupport = -> [Pocket044]
  ExternalGeometry = -> [Pocket044]
  FullyConstrained = true
  MakeInternals = false
  MapMode = 5
  Placement = pos=(0,0,-6.8) rot=(1,0,0;3.14159rad)
  sketch-geometry (2):
    g0: Circle CenterX=20.6 CenterY=16.25 CenterZ=0 NormalX=0 NormalY=0 NormalZ=1 AngleXU=0 Radius=3.55
    g1: Circle CenterX=20.6 CenterY=16.25 CenterZ=0 NormalX=0 NormalY=0 NormalZ=1 AngleXU=0 Radius=2.3
  constraints (4):
    c: Coincident(g0,g-3)
    c: Equal(g0,g-3)
    c: Coincident(g1,g0)
    c: Diameter(g1) = 4.6
FEATURE [PartDesign::Pad] Pad104
  BaseFeature = -> Pocket044
  Direction = (0,0,-1)
  Length = 2
  Length2 = 10
  Profile = -> Sketch137
  ReferenceAxis = -> Sketch137 [N_Axis]
  Refine = true
  Reversed = true
  Suppressed = false
  Type = 0
FEATURE [Sketcher::SketchObject] Sketch138
  ArcFitTolerance = 1e-06
  AttachmentSupport = -> [Pad104]
  ExternalGeometry = -> [Pad104]
  FullyConstrained = true
  MakeInternals = false
  MapMode = 5
  Placement = pos=(0,0,-4.8) rot=(0,0,1;0rad)
  sketch-geometry (16):
    g0: LineSegment StartX=20.1 StartY=-12.7354 StartZ=0 EndX=20.1 EndY=-14.005 EndZ=0
    g1: LineSegment StartX=21.1 StartY=-12.7354 StartZ=0 EndX=21.1 EndY=-14.005 EndZ=0
    g2: LineSegment StartX=22.845 StartY=-15.75 StartZ=0 EndX=24.1147 EndY=-15.75 EndZ=0
    g3: LineSegment StartX=22.845 StartY=-16.75 StartZ=0 EndX=24.1147 EndY=-16.75 EndZ=0
    g4: LineSegment StartX=18.355 StartY=-15.75 StartZ=0 EndX=17.0854 EndY=-15.75 EndZ=0
    g5: LineSegment StartX=18.355 StartY=-16.75 StartZ=0 EndX=17.0854 EndY=-16.75 EndZ=0
    g6: LineSegment StartX=20.1 StartY=-18.495 StartZ=0 EndX=20.1 EndY=-19.7646 EndZ=0
    g7: LineSegment StartX=21.1 StartY=-18.495 StartZ=0 EndX=21.1 EndY=-19.7646 EndZ=0
    g8: ArcOfCircle CenterX=20.6 CenterY=-16.25 CenterZ=0 NormalX=0 NormalY=0 NormalZ=1 AngleXU=0 Radius=3.55 StartAngle=3.00028 EndAngle=3.28291
    g9: ArcOfCircle CenterX=20.6 CenterY=-16.25 CenterZ=0 NormalX=0 NormalY=0 NormalZ=1 AngleXU=0 Radius=2.3 StartAngle=2.92245 EndAngle=3.36073
    g10: ArcOfCircle CenterX=20.6 CenterY=-16.25 CenterZ=0 NormalX=0 NormalY=0 NormalZ=1 AngleXU=0 Radius=3.55 StartAngle=1.42948 EndAngle=1.71211
    g11: ArcOfCircle CenterX=20.6 CenterY=-16.25 CenterZ=0 NormalX=0 NormalY=0 NormalZ=1 AngleXU=0 Radius=2.3 StartAngle=1.35166 EndAngle=1.78994
    g12: ArcOfCircle CenterX=20.6 CenterY=-16.25 CenterZ=0 NormalX=0 NormalY=0 NormalZ=1 AngleXU=0 Radius=2.3 StartAngle=6.06404 EndAngle=6.50233
    g13: ArcOfCircle CenterX=20.6 CenterY=-16.25 CenterZ=0 NormalX=0 NormalY=0 NormalZ=1 AngleXU=0 Radius=3.55 StartAngle=6.14187 EndAngle=6.4245
    g14: ArcOfCircle CenterX=20.6 CenterY=-16.25 CenterZ=0 NormalX=0 NormalY=0 NormalZ=1 AngleXU=0 Radius=2.3 StartAngle=4.49325 EndAngle=4.93153
    g15: ArcOfCircle CenterX=20.6 CenterY=-16.25 CenterZ=0 NormalX=0 NormalY=0 NormalZ=1 AngleXU=0 Radius=3.55 StartAngle=4.57107 EndAngle=4.8537
  constraints (56):
    c: PointOnObject(g0,g-4)
    c: PointOnObject(g0,g-3)
    c: Vertical(g0)
    c: PointOnObject(g1,g-4)
    c: PointOnObject(g1,g-3)
    c: Vertical(g1)
    c: PointOnObject(g2,g-3)
    c: PointOnObject(g2,g-4)
    c: Horizontal(g2)
    c: PointOnObject(g3,g-3)
    c: PointOnObject(g3,g-4)
    c: Horizontal(g3)
    c: PointOnObject(g4,g-3)
    c: PointOnObject(g4,g-4)
    c: Horizontal(g4)
    c: PointOnObject(g5,g-3)
    c: PointOnObject(g5,g-4)
    c: Horizontal(g5)
    c: PointOnObject(g6,g-3)
    c: PointOnObject(g6,g-4)
    c: Vertical(g6)
    c: PointOnObject(g7,g-3)
    c: PointOnObject(g7,g-4)
    c: Vertical(g7)
    c: DistanceY(g-4,g4) = 0.5
    c: DistanceY(g5,g-4) = 0.5
    c: DistanceY(g-4,g2) = 0.5
    c: DistanceY(g3,g-4) = 0.5
    c: DistanceX(g0,g-4) = 0.5
    c: DistanceX(g6,g-4) = 0.5
    c: DistanceX(g-4,g7) = 0.5
    c: DistanceX(g-4,g1) = 0.5
    c: Coincident(g8,g4)
    c: Coincident(g8,g5)
    c: Tangent(g8,g-4)
    c: Coincident(g9,g5)
    c: Coincident(g9,g4)
    c: Tangent(g9,g-3)
    c: Coincident(g10,g0)
    c: Coincident(g10,g1)
    c: Tangent(g10,g-4)
    c: Coincident(g11,g0)
    c: Coincident(g11,g1)
    c: Tangent(g11,g-3)
    c: Coincident(g12,g2)
    c: Coincident(g12,g3)
    c: Tangent(g12,g-3)
    c: Coincident(g13,g2)
    c: Coincident(g13,g3)
    c: Tangent(g13,g-4)
    c: Coincident(g14,g6)
    c: Coincident(g14,g7)
    c: Tangent(g14,g-3)
    c: Coincident(g15,g6)
    c: Coincident(g15,g7)
    c: Tangent(g15,g-4)
FEATURE [PartDesign::Pad] Pad105
  BaseFeature = -> Pad104
  Direction = (0,0,1)
  Length = 1.4
  Length2 = 10
  Profile = -> Sketch138
  ReferenceAxis = -> Sketch138 [N_Axis]
  Refine = true
  Suppressed = false
  Type = 0
FEATURE [PartDesign::Chamfer] Chamfer002
  Angle = 45
  Base = -> Pad105 [Edge59,Edge61,Edge67,Edge70,Edge43,Edge45,Edge51,Edge52]
  BaseFeature = -> Pad105
  ChamferType = 0
  FlipDirection = false
  Refine = true
  Size = 0.4
  Size2 = 1
  SupportTransform = false
  Suppressed = false
  UseAllEdges = false
FEATURE [Sketcher::SketchObject] Sketch139
  ArcFitTolerance = 1e-06
  AttachmentSupport = -> [Chamfer002]
  ExternalGeometry = -> [Chamfer002]
  FullyConstrained = true
  MakeInternals = false
  MapMode = 5
  Placement = pos=(0,0,-3.4) rot=(0,0,1;0rad)
  sketch-geometry (1):
    g0: Circle CenterX=20.6 CenterY=-16.25 CenterZ=0 NormalX=0 NormalY=0 NormalZ=1 AngleXU=0 Radius=3.55
  constraints (2):
    c: Coincident(g0,g-3)
    c: Equal(g0,g-3)
FEATURE [PartDesign::Pocket] Pocket045
  BaseFeature = -> Chamfer002
  Direction = (0,0,-1)
  Length = 0.1
  Length2 = 5
  Profile = -> Sketch139
  ReferenceAxis = -> Sketch139 [N_Axis]
  Refine = true
  Suppressed = false
  Type = 0
FEATURE [Sketcher::SketchObject] Sketch140
  ArcFitTolerance = 1e-06
  AttachmentSupport = -> [Pocket045]
  ExternalGeometry = -> [Pocket045]
  FullyConstrained = true
  MakeInternals = false
  MapMode = 5
  Placement = pos=(0,0,-13.2) rot=(1,0,0;3.14159rad)
  sketch-geometry (4):
    g0: LineSegment StartX=50.6 StartY=21.9 StartZ=0 EndX=50.6 EndY=10.1 EndZ=0
    g1: LineSegment StartX=50.6 StartY=10.1 StartZ=0 EndX=56.6 EndY=10.1 EndZ=0
    g2: LineSegment StartX=56.6 StartY=10.1 StartZ=0 EndX=56.6 EndY=21.9 EndZ=0
    g3: LineSegment StartX=56.6 StartY=21.9 StartZ=0 EndX=50.6 EndY=21.9 EndZ=0
  constraints (13):
    c: Coincident(g0,g1)
    c: Coincident(g1,g2)
    c: Coincident(g2,g3)
    c: Coincident(g3,g0)
    c: Vertical(g0)
    c: Vertical(g2)
    c: Horizontal(g1)
    c: Horizontal(g3)
    c: PointOnObject(g0,g-3)
    c: DistanceY(g2,g2) = 11.8
    c: DistanceY(g-3,g-3) = 20
    c: DistanceY(g0,g-3) = 4.1
    c: DistanceX(g3,g3) = 6
FEATURE [PartDesign::Pad] Pad106
  BaseFeature = -> Pocket045
  Direction = (0,0,-1)
  Length = 3
  Length2 = 10
  Profile = -> Sketch140
  ReferenceAxis = -> Sketch140 [N_Axis]
  Refine = true
  Reversed = true
  Suppressed = false
  Type = 0
FEATURE [Sketcher::SketchObject] Sketch141
  ArcFitTolerance = 1e-06
  AttachmentSupport = -> [Pad106]
  ExternalGeometry = -> [Pad106]
  FullyConstrained = true
  MakeInternals = false
  MapMode = 5
  Placement = pos=(0,0,-13.2) rot=(1,0,0;3.14159rad)
  sketch-geometry (4):
    g0: LineSegment StartX=55.2 StartY=20 StartZ=0 EndX=55.2 EndY=12 EndZ=0
    g1: LineSegment StartX=55.2 StartY=12 StartZ=0 EndX=58 EndY=12 EndZ=0
    g2: LineSegment StartX=58 StartY=12 StartZ=0 EndX=58 EndY=20 EndZ=0
    g3: LineSegment StartX=58 StartY=20 StartZ=0 EndX=55.2 EndY=20 EndZ=0
  constraints (13):
    c: Coincident(g0,g1)
    c: Coincident(g1,g2)
    c: Coincident(g2,g3)
    c: Coincident(g3,g0)
    c: Vertical(g0)
    c: Vertical(g2)
    c: Horizontal(g1)
    c: Horizontal(g3)
    c: DistanceY(g2,g2) = 8
    c: DistanceY(g-5,g-5) = 11.8
    c: DistanceY(g2,g-5) = 1.9
    c: DistanceX(g3,g3) = 2.8
    c: DistanceX(g-5,g2) = 1.4
FEATURE [PartDesign::Pad] Pad107
  BaseFeature = -> Pad106
  Direction = (0,0,-1)
  Length = 1.5
  Length2 = 10
  Profile = -> Sketch141
  ReferenceAxis = -> Sketch141 [N_Axis]
  Refine = true
  Suppressed = false
  Type = 0
FEATURE [Sketcher::SketchObject] Sketch142
  ArcFitTolerance = 1e-06
  AttachmentSupport = -> [Pad107]
  ExternalGeometry = -> [Pad107]
  FullyConstrained = true
  MakeInternals = false
  MapMode = 5
  Placement = pos=(0,-21.9,0) rot=(1,0,0;1.5708rad)
  sketch-geometry (2):
    g0: ArcOfCircle CenterX=53.7 CenterY=-13.2 CenterZ=0 NormalX=0 NormalY=0 NormalZ=1 AngleXU=0 Radius=1.5 StartAngle=-1.8e-15 EndAngle=3.14159
    g1: LineSegment StartX=52.2 StartY=-13.2 StartZ=0 EndX=55.2 EndY=-13.2 EndZ=0
  constraints (6):
    c: Coincident(g0,g-4)
    c: PointOnObject(g0,g-3)
    c: PointOnObject(g0,g-3)
    c: Diameter(g0) = 3
    c: Coincident(g1,g0)
    c: Coincident(g1,g0)
FEATURE [PartDesign::Pocket] Pocket046
  BaseFeature = -> Pad107
  Direction = (0,1,-2e-16)
  Length = 12
  Length2 = 5
  Profile = -> Sketch142
  ReferenceAxis = -> Sketch142 [N_Axis]
  Refine = true
  Suppressed = false
  Type = 0
FEATURE [Sketcher::SketchObject] Sketch143
  ArcFitTolerance = 1e-06
  AttachmentSupport = -> [Pocket046]
  ExternalGeometry = -> [Pocket046]
  FullyConstrained = true
  MakeInternals = false
  MapMode = 5
  Placement = pos=(0,-21.9,0) rot=(1,0,0;1.5708rad)
  sketch-geometry (3):
    g0: ArcOfCircle CenterX=53.7 CenterY=-13.1017 CenterZ=0 NormalX=0 NormalY=0 NormalZ=1 AngleXU=0 Radius=2.90167 StartAngle=6.24929 EndAngle=7.85398
    g1: LineSegment StartX=53.7 StartY=-10.2 StartZ=0 EndX=56.6 EndY=-10.2 EndZ=0
    g2: LineSegment StartX=56.6 StartY=-10.2 StartZ=0 EndX=56.6 EndY=-13.2 EndZ=0
  constraints (7):
    c: Coincident(g0,g-4)
    c: PointOnObject(g0,g-5)
    c: DistanceX(g-3,g0) = 0
    c: Tangent(g1,g0) = 1.5708
    c: Coincident(g1,g-5)
    c: Coincident(g2,g0)
    c: Coincident(g2,g1)
FEATURE [PartDesign::Pocket] Pocket047
  BaseFeature = -> Pocket046
  Direction = (0,1,-2e-16)
  Length = 12
  Length2 = 5
  Profile = -> Sketch143
  ReferenceAxis = -> Sketch143 [N_Axis]
  Refine = true
  Suppressed = false
  Type = 0
FEATURE [PartDesign::Fillet] Fillet010
  Base = -> Pocket047 [Edge53,Edge50,Edge47,Edge48,Edge4,Edge26]
  BaseFeature = -> Pocket047
  Radius = 1
  Refine = true
  SupportTransform = false
  Suppressed = false
  UseAllEdges = false
FEATURE [Sketcher::SketchObject] Sketch144
  ArcFitTolerance = 1e-06
  AttachmentSupport = -> [Fillet010]
  ExternalGeometry = -> [Fillet010]
  FullyConstrained = true
  MakeInternals = false
  MapMode = 5
  Placement = pos=(0,0,-10.2) rot=(0,0,1;0rad)
  sketch-geometry (20):
    g0: LineSegment StartX=37.6 StartY=-11.25 StartZ=0 EndX=37.6 EndY=-8 EndZ=0
    g1: LineSegment StartX=37.6 StartY=-8 StartZ=0 EndX=20.6 EndY=-8 EndZ=0
    g2: LineSegment StartX=37.6 StartY=-21.25 StartZ=0 EndX=37.6 EndY=-24 EndZ=0
    g3: LineSegment StartX=37.6 StartY=-24 StartZ=0 EndX=20.6 EndY=-24 EndZ=0
    g4: LineSegment StartX=37.6 StartY=-21.25 StartZ=0 EndX=20.6 EndY=-21.25 EndZ=0
    g5: LineSegment StartX=37.6 StartY=-11.25 StartZ=0 EndX=20.6 EndY=-11.25 EndZ=0
    g6: LineSegment [constr] StartX=20.6 StartY=-26 StartZ=0 EndX=20.6 EndY=-24 EndZ=0
    g7: LineSegment [constr] StartX=20.6 StartY=-8 StartZ=0 EndX=20.6 EndY=-6 EndZ=0
    g8: ArcOfCircle CenterX=20.6 CenterY=-16 CenterZ=0 NormalX=0 NormalY=0 NormalZ=1 AngleXU=0 Radius=8 StartAngle=1.5708 EndAngle=4.71239
    g9: ArcOfCircle CenterX=20.6 CenterY=-16.25 CenterZ=0 NormalX=0 NormalY=0 NormalZ=1 AngleXU=0 Radius=5 StartAngle=1.5708 EndAngle=4.71239
    g10: LineSegment StartX=24.6 StartY=-13.25 StartZ=0 EndX=37.6 EndY=-13.25 EndZ=0
    g11: LineSegment StartX=37.6 StartY=-13.25 StartZ=0 EndX=37.6 EndY=-15.25 EndZ=0
    g12: LineSegment StartX=37.6 StartY=-15.25 StartZ=0 EndX=25.499 EndY=-15.25 EndZ=0
    g13: LineSegment StartX=25.499 StartY=-17.25 StartZ=0 EndX=37.6 EndY=-17.25 EndZ=0
    g14: LineSegment StartX=37.6 StartY=-17.25 StartZ=0 EndX=37.6 EndY=-19.25 EndZ=0
    g15: LineSegment StartX=37.6 StartY=-19.25 StartZ=0 EndX=24.6 EndY=-19.25 EndZ=0
    g16: ArcOfCircle CenterX=20.6 CenterY=-16.25 CenterZ=0 NormalX=0 NormalY=0 NormalZ=1 AngleXU=0 Radius=5 StartAngle=5.63968 EndAngle=6.08183
    g17: ArcOfCircle CenterX=20.6001 CenterY=-16.25 CenterZ=0 NormalX=0 NormalY=0 NormalZ=1 AngleXU=0 Radius=4.99998 StartAngle=0.201357 EndAngle=0.643502
    g18: LineSegment [constr] StartX=37.6 StartY=-11.25 StartZ=0 EndX=37.6 EndY=-13.25 EndZ=0
    g19: LineSegment [constr] StartX=37.6 StartY=-15.25 StartZ=0 EndX=37.6 EndY=-17.25 EndZ=0
  constraints (61):
    c: Vertical(g0)
    c: Coincident(g1,g0)
    c: Horizontal(g1)
    c: Vertical(g2)
    c: Coincident(g3,g2)
    c: Horizontal(g3)
    c: Coincident(g4,g2)
    c: Horizontal(g4)
    c: Coincident(g5,g0)
    c: Horizontal(g5)
    c: DistanceY(g1,g-4) = 2
    c: DistanceY(g-4,g3) = 2
    c: Coincident(g6,g-4)
    c: Coincident(g6,g3)
    c: Vertical(g6)
    c: Coincident(g7,g1)
    c: Coincident(g7,g-4)
    c: Vertical(g7)
    c: Coincident(g8,g3)
    c: Coincident(g8,g1)
    c: DistanceX(g8,g1) = 0
    c: Coincident(g9,g4)
    c: Coincident(g5,g9)
    c: DistanceX(g4,g3) = 0
    c: DistanceX(g5,g1) = 0
    c: Radius(g9) = 5
    c: DistanceX(g0,g-5) = 13
    c: DistanceX(g2,g-6) = 13
    c: DistanceX(g9,g8) = 0
    c: DistanceY(g0,g0) = 3.25
    c: PointOnObject(g10,g-7)
    c: Horizontal(g10)
    c: Coincident(g11,g10)
    c: Vertical(g11)
    c: Coincident(g12,g11)
    c: PointOnObject(g12,g-7)
    c: Horizontal(g12)
    c: PointOnObject(g13,g-7)
    c: Horizontal(g13)
    c: Coincident(g14,g13)
    c: Vertical(g14)
    c: Coincident(g15,g14)
    c: PointOnObject(g15,g-7)
    c: Horizontal(g15)
    c: Coincident(g16,g15)
    c: Coincident(g16,g13)
    c: Tangent(g16,g-7)
    c: Coincident(g17,g12)
    c: Coincident(g17,g10)
    c: Tangent(g17,g-7)
    c: DistanceY(g11,g11) = 2
    c: DistanceY(g14,g14) = 2
    c: Coincident(g18,g0)
    c: Coincident(g18,g10)
    c: Coincident(g19,g11)
    c: Coincident(g19,g13)
    c: Vertical(g18)
    c: Vertical(g19)
    c: DistanceY(g13,g11) = 2
    c: DistanceY(g10,g0) = 2
    c: DistanceY(g2,g14) = 2
FEATURE [PartDesign::Pocket] Pocket048
  BaseFeature = -> Fillet010
  Direction = (0,0,-1)
  Length = 1.5
  Length2 = 5
  Profile = -> Sketch144
  ReferenceAxis = -> Sketch144 [N_Axis]
  Refine = true
  Suppressed = false
  Type = 0
FEATURE [Sketcher::SketchObject] Sketch145
  ArcFitTolerance = 1e-06
  AttachmentSupport = -> [Pocket048]
  ExternalGeometry = -> [Pocket048]
  FullyConstrained = true
  MakeInternals = false
  MapMode = 5
  Placement = pos=(0,0,-13.2) rot=(1,0,0;3.14159rad)
  sketch-geometry (2):
    g0: Circle CenterX=46.45 CenterY=16 CenterZ=0 NormalX=0 NormalY=0 NormalZ=1 AngleXU=0 Radius=2.35
    g1: LineSegment [constr] StartX=46.45 StartY=16 StartZ=0 EndX=48.8 EndY=16 EndZ=0
  constraints (7):
    c: Diameter(g0) = 4.7
    c: DistanceY(g-4,g-3) = 20
    c: DistanceY(g0,g-3) = 10
    c: Coincident(g1,g0)
    c: PointOnObject(g1,g0)
    c: Horizontal(g1)
    c: DistanceX(g1,g-5) = 9.2
FEATURE [PartDesign::Pad] Pad108
  BaseFeature = -> Pocket048
  Direction = (0,0,-1)
  Length = 2
  Length2 = 10
  Profile = -> Sketch145
  ReferenceAxis = -> Sketch145 [N_Axis]
  Refine = true
  Suppressed = false
  Type = 0
FEATURE [Sketcher::SketchObject] Sketch146
  ArcFitTolerance = 1e-06
  AttachmentSupport = -> [Pad108]
  ExternalGeometry = -> [Pad108]
  FullyConstrained = true
  MakeInternals = false
  MapMode = 5
  Placement = pos=(0,0,-15.2) rot=(1,0,0;3.14159rad)
  sketch-geometry (1):
    g0: Circle CenterX=46.45 CenterY=16 CenterZ=0 NormalX=0 NormalY=0 NormalZ=1 AngleXU=0 Radius=0.75
  constraints (2):
    c: Coincident(g0,g-3)
    c: Radius(g0) = 0.75
FEATURE [PartDesign::Pocket] Pocket049
  BaseFeature = -> Pad108
  Direction = (0,0,1)
  Length = 5
  Length2 = 5
  Profile = -> Sketch146
  ReferenceAxis = -> Sketch146 [N_Axis]
  Refine = true
  Suppressed = false
  Type = 0
FEATURE [Sketcher::SketchObject] Sketch147
  ArcFitTolerance = 1e-06
  AttachmentSupport = -> [Pocket049]
  ExternalGeometry = -> [Pocket049]
  FullyConstrained = true
  MakeInternals = false
  MapMode = 5
  Placement = pos=(0,-26,0) rot=(1,0,0;1.5708rad)
  sketch-geometry (2):
    g0: ArcOfCircle CenterX=39.55 CenterY=-13.2 CenterZ=0 NormalX=0 NormalY=0 NormalZ=1 AngleXU=0 Radius=1.25 StartAngle=7e-16 EndAngle=3.14159
    g1: LineSegment StartX=40.8 StartY=-13.2 StartZ=0 EndX=38.3 EndY=-13.2 EndZ=0
  constraints (7):
    c: PointOnObject(g0,g-3)
    c: PointOnObject(g0,g-3)
    c: Diameter(g0) = 2.5
    c: DistanceX(g0,g-4) = 9.8
    c: PointOnObject(g0,g-3)
    c: Coincident(g1,g0)
    c: Coincident(g1,g0)
FEATURE [PartDesign::Pocket] Pocket050
  BaseFeature = -> Pocket049
  Direction = (0,1,-2e-16)
  Length = 18.5
  Length2 = 5
  Profile = -> Sketch147
  ReferenceAxis = -> Sketch147 [N_Axis]
  Refine = true
  Suppressed = false
  Type = 0
FEATURE [Sketcher::SketchObject] Sketch148
  ArcFitTolerance = 1e-06
  AttachmentSupport = -> [Pocket050]
  ExternalGeometry = -> [Pocket050]
  FullyConstrained = true
  MakeInternals = false
  MapMode = 5
  Placement = pos=(0,-26,0) rot=(1,0,0;1.5708rad)
  sketch-geometry (2):
    g0: ArcOfCircle CenterX=39.55 CenterY=-13.2 CenterZ=0 NormalX=0 NormalY=0 NormalZ=1 AngleXU=0 Radius=1.25 StartAngle=-1.8e-15 EndAngle=3.14159
    g1: LineSegment StartX=38.3 StartY=-13.2 StartZ=0 EndX=40.8 EndY=-13.2 EndZ=0
  constraints (4):
    c: Tangent(g0,g-3) = -1.5708
    c: Coincident(g0,g-3)
    c: Coincident(g1,g0)
    c: Coincident(g1,g0)
FEATURE [PartDesign::Pad] Pad109
  BaseFeature = -> Pocket050
  Direction = (0,-1,2e-16)
  Length = 1.5
  Length2 = 10
  Profile = -> Sketch148
  ReferenceAxis = -> Sketch148 [N_Axis]
  Refine = true
  Reversed = true
  Suppressed = false
  Type = 0
FEATURE [Sketcher::SketchObject] Sketch149
  ArcFitTolerance = 1e-06
  AttachmentSupport = -> [Pad109]
  ExternalGeometry = -> [Pad109]
  FullyConstrained = true
  MakeInternals = false
  MapMode = 5
  Placement = pos=(0,0,-13.2) rot=(1,0,0;3.14159rad)
  sketch-geometry (13):
    g0: LineSegment StartX=52.2 StartY=18.4 StartZ=0 EndX=52.2 EndY=13.6 EndZ=0
    g1: LineSegment StartX=49.1 StartY=11.6 StartZ=0 EndX=49.1 EndY=7.5 EndZ=0
    g2: LineSegment StartX=49.1 StartY=7.5 StartZ=0 EndX=42.3 EndY=7.5 EndZ=0
    g3: LineSegment StartX=42.3 StartY=7.5 StartZ=0 EndX=42.3 EndY=24.5 EndZ=0
    g4: LineSegment StartX=42.3 StartY=24.5 StartZ=0 EndX=49.1 EndY=24.5 EndZ=0
    g5: LineSegment StartX=49.1 StartY=24.5 StartZ=0 EndX=49.1 EndY=20.4 EndZ=0
    g6: Circle CenterX=46.45 CenterY=16 CenterZ=0 NormalX=0 NormalY=0 NormalZ=1 AngleXU=0 Radius=2.35
    g7: LineSegment StartX=52.2 StartY=18.4 StartZ=0 EndX=50.7 EndY=18.4 EndZ=0
    g8: LineSegment StartX=50.7 StartY=18.4 StartZ=0 EndX=50.7 EndY=20.4 EndZ=0
    g9: LineSegment StartX=50.7 StartY=20.4 StartZ=0 EndX=49.1 EndY=20.4 EndZ=0
    g10: LineSegment StartX=52.2 StartY=13.6 StartZ=0 EndX=50.7 EndY=13.6 EndZ=0
    g11: LineSegment StartX=50.7 StartY=13.6 StartZ=0 EndX=50.7 EndY=11.6 EndZ=0
    g12: LineSegment StartX=50.7 StartY=11.6 StartZ=0 EndX=49.1 EndY=11.6 EndZ=0
  constraints (38):
    c: PointOnObject(g0,g-10)
    c: PointOnObject(g0,g-10)
    c: Vertical(g1)
    c: Coincident(g2,g1)
    c: Horizontal(g2)
    c: Coincident(g3,g2)
    c: Vertical(g3)
    c: Coincident(g4,g3)
    c: Horizontal(g4)
    c: Coincident(g5,g4)
    c: Vertical(g5)
    c: Coincident(g6,g-11)
    c: Equal(g6,g-11)
    c: Coincident(g7,g0)
    c: Horizontal(g7)
    c: Coincident(g8,g7)
    c: Vertical(g8)
    c: Coincident(g9,g8)
    c: Coincident(g9,g5)
    c: Horizontal(g9)
    c: Coincident(g10,g0)
    c: Horizontal(g10)
    c: Coincident(g11,g10)
    c: Vertical(g11)
    c: Coincident(g12,g11)
    c: Coincident(g12,g1)
    c: Horizontal(g12)
    c: DistanceX(g10,g10) = 1.5
    c: DistanceX(g7,g7) = 1.5
    c: DistanceX(g-3,g2) = 1.5
    c: DistanceY(g-9,g2) = 1.5
    c: DistanceY(g4,g-4) = 1.5
    c: DistanceX(g4,g-5) = 1.5
    c: DistanceX(g1,g-8) = 1.5
    c: DistanceY(g-8,g11) = 1.5
    c: DistanceY(g8,g-6) = 1.5
    c: DistanceY(g-10,g0) = 3.5
    c: DistanceY(g0,g-10) = 3.5
FEATURE [PartDesign::Pocket] Pocket051
  BaseFeature = -> Pad109
  Direction = (0,0,1)
  Length = 1.5
  Length2 = 5
  Profile = -> Sketch149
  ReferenceAxis = -> Sketch149 [N_Axis]
  Refine = true
  Suppressed = false
  Type = 0
FEATURE [PartDesign::Pocket] Pocket052
  BaseFeature = -> Pocket051
  Direction = (1,3e-15,0)
  Length = 1.5
  Length2 = 5
  Profile = -> Pocket051 [Face84]
  Refine = true
  Suppressed = false
  Type = 0
FEATURE [PartDesign::Fillet] Fillet011
  Base = -> Pocket052 [Edge223,Edge219,Edge206,Edge209]
  BaseFeature = -> Pocket052
  Radius = 0.5
  Refine = true
  SupportTransform = false
  Suppressed = false
  UseAllEdges = false
FEATURE [Sketcher::SketchObject] Sketch150
  ArcFitTolerance = 1e-06
  AttachmentSupport = -> [Fillet011]
  ExternalGeometry = -> [Fillet011]
  FullyConstrained = true
  MakeInternals = false
  MapMode = 5
  Placement = pos=(0,0,-11.7) rot=(1,0,0;3.14159rad)
  sketch-geometry (4):
    g0: LineSegment StartX=52.2 StartY=18.4 StartZ=0 EndX=52.2 EndY=13.6 EndZ=0
    g1: LineSegment StartX=52.2 StartY=13.6 StartZ=0 EndX=55.2 EndY=13.6 EndZ=0
    g2: LineSegment StartX=55.2 StartY=13.6 StartZ=0 EndX=55.2 EndY=18.4 EndZ=0
    g3: LineSegment StartX=55.2 StartY=18.4 StartZ=0 EndX=52.2 EndY=18.4 EndZ=0
  constraints (10):
    c: Coincident(g0,g1)
    c: Coincident(g1,g2)
    c: Coincident(g2,g3)
    c: Coincident(g3,g0)
    c: Vertical(g2)
    c: Horizontal(g1)
    c: Horizontal(g3)
    c: Coincident(g0,g-3)
    c: PointOnObject(g1,g-5)
    c: Coincident(g0,g-4)
FEATURE [PartDesign::Pad] Pad110
  BaseFeature = -> Fillet011
  Direction = (0,0,-1)
  Length = 0.1
  Length2 = 10
  Profile = -> Sketch150
  ReferenceAxis = -> Sketch150 [N_Axis]
  Refine = true
  Suppressed = false
  Type = 0
FEATURE [Sketcher::SketchObject] Sketch151
  ArcFitTolerance = 1e-06
  AttachmentSupport = -> [Pad110]
  ExternalGeometry = -> [Pad110]
  FullyConstrained = true
  MakeInternals = false
  MapMode = 5
  Placement = pos=(0,0,-13.2) rot=(1,0,0;3.14159rad)
  sketch-geometry (8):
    g0: LineSegment StartX=31.6 StartY=26 StartZ=0 EndX=31.6 EndY=20 EndZ=0
    g1: LineSegment StartX=31.6 StartY=20 StartZ=0 EndX=35.6 EndY=20 EndZ=0
    g2: LineSegment StartX=35.6 StartY=20 StartZ=0 EndX=35.6 EndY=26 EndZ=0
    g3: LineSegment StartX=35.6 StartY=26 StartZ=0 EndX=31.6 EndY=26 EndZ=0
    g4: LineSegment StartX=31.6 StartY=6 StartZ=0 EndX=35.6 EndY=6 EndZ=0
    g5: LineSegment StartX=35.6 StartY=6 StartZ=0 EndX=35.6 EndY=12 EndZ=0
    g6: LineSegment StartX=35.6 StartY=12 StartZ=0 EndX=31.6 EndY=12 EndZ=0
    g7: LineSegment StartX=31.6 StartY=12 StartZ=0 EndX=31.6 EndY=6 EndZ=0
  constraints (24):
    c: Coincident(g0,g1)
    c: Coincident(g1,g2)
    c: Coincident(g2,g3)
    c: Coincident(g3,g0)
    c: Vertical(g0)
    c: Vertical(g2)
    c: Horizontal(g1)
    c: Horizontal(g3)
    c: PointOnObject(g0,g-3)
    c: Coincident(g4,g5)
    c: Coincident(g5,g6)
    c: Coincident(g6,g7)
    c: Coincident(g7,g4)
    c: Horizontal(g4)
    c: Horizontal(g6)
    c: Vertical(g5)
    c: Vertical(g7)
    c: PointOnObject(g4,g-4)
    c: DistanceY(g2,g2) = 6
    c: DistanceY(g5,g5) = 6
    c: DistanceX(g1,g1) = 4
    c: DistanceX(g6,g6) = 4
    c: DistanceX(g1,g5) = 0
    c: DistanceX(g0,g-5) = 19
FEATURE [PartDesign::Body] Body005  label="Chest_Plate"
  AllowCompound = false
  Group = -> [Binder002,Sketch133,Pad102,Sketch134,Pocket043,Sketch135,Pad103,Sketch136,Pocket044,Sketch137,Pad104,Sketch138,Pad105,Chamfer002,Sketch139,Pocket045,Sketch140,Pad106,Sketch141,Pad107,Sketch142,Pocket046,Sketch143,Pocket047,Fillet010,Sketch144,Pocket048,Sketch145,Pad108,Sketch146,Pocket049,Sketch147,Pocket050,Sketch148,Pad109,Sketch149,Pocket051,Pocket052,Fillet011,Sketch150,Pad110,Sketch151,+9 more]
  Origin = -> Origin005
  Tip = -> Pad113
COMPONENT P6 — recipe-attached ("Front_Cover", modeled in this document).
Construction recipe (the document's own serialized feature program — sketch geometry with constraints, then the solid features built on it; lengths are millimeters unless a unit is written):

FEATURE [PartDesign::SubShapeBinder] Binder003
  BindCopyOnChange = 0
  BindMode = 2
  ClaimChildren = false
  Context = -> Body006 [Binder003.]
  Fuse = false
  MakeFace = true
  OffsetFill = false
  OffsetIntersection = false
  OffsetJoinType = 0
  OffsetOpenResult = false
  PartialLoad = false
  Refine = true
  Relative = true
  _Version = 2
FEATURE [Sketcher::SketchObject] Sketch155
  ArcFitTolerance = 1e-06
  AttachmentSupport = -> [Binder003]
  ExternalGeometry = -> [Binder003]
  FullyConstrained = true
  MakeInternals = false
  MapMode = 5
  Placement = pos=(0,0,-13.2) rot=(1,0,0;3.14159rad)
  sketch-geometry (28):
    g0: LineSegment StartX=50.6 StartY=21.9 StartZ=0 EndX=58.1 EndY=21.9 EndZ=0
    g1: LineSegment StartX=59.1 StartY=20.9 StartZ=0 EndX=59.1 EndY=11.1 EndZ=0
    g2: LineSegment StartX=58.1 StartY=10.1 StartZ=0 EndX=50.6 EndY=10.1 EndZ=0
    g3: LineSegment StartX=50.6 StartY=10.1 StartZ=0 EndX=50.6 EndY=7 EndZ=0
    g4: LineSegment StartX=49.6 StartY=6 StartZ=0 EndX=36.4 EndY=6 EndZ=0
    g5: LineSegment StartX=35.9 StartY=6.5 StartZ=0 EndX=35.9 EndY=11.4 EndZ=0
    g6: LineSegment StartX=36.4 StartY=11.9 StartZ=0 EndX=42.3 EndY=11.9 EndZ=0
    g7: LineSegment StartX=42.3 StartY=11.9 StartZ=0 EndX=42.3 EndY=20.1 EndZ=0
    g8: LineSegment StartX=42.3 StartY=20.1 StartZ=0 EndX=36.4 EndY=20.1 EndZ=0
    g9: LineSegment StartX=35.9 StartY=20.6 StartZ=0 EndX=35.9 EndY=25.5 EndZ=0
    g10: LineSegment StartX=36.4 StartY=26 StartZ=0 EndX=49.6 EndY=26 EndZ=0
    g11: LineSegment StartX=50.6 StartY=25 StartZ=0 EndX=50.6 EndY=21.9 EndZ=0
    g12: ArcOfCircle CenterX=49.6 CenterY=25 CenterZ=0 NormalX=0 NormalY=0 NormalZ=1 AngleXU=0 Radius=1 StartAngle=-1.8e-15 EndAngle=1.5708
    g13: GeomPoint [constr] X=50.6 Y=26 Z=0
    g14: ArcOfCircle CenterX=49.6 CenterY=7 CenterZ=0 NormalX=0 NormalY=0 NormalZ=1 AngleXU=0 Radius=1 StartAngle=4.71239 EndAngle=6.28319
    g15: GeomPoint [constr] X=50.6 Y=6 Z=0
    g16: ArcOfCircle CenterX=58.1 CenterY=11.1 CenterZ=0 NormalX=0 NormalY=0 NormalZ=1 AngleXU=0 Radius=1 StartAngle=4.71239 EndAngle=6.28319
    g17: GeomPoint [constr] X=59.1 Y=10.1 Z=0
    g18: ArcOfCircle CenterX=58.1 CenterY=20.9 CenterZ=0 NormalX=0 NormalY=0 NormalZ=1 AngleXU=0 Radius=1 StartAngle=1.3e-15 EndAngle=1.5708
    g19: GeomPoint [constr] X=59.1 Y=21.9 Z=0
    g20: ArcOfCircle CenterX=36.4 CenterY=6.5 CenterZ=0 NormalX=0 NormalY=0 NormalZ=1 AngleXU=0 Radius=0.5 StartAngle=3.14159 EndAngle=4.71239
    g21: GeomPoint [constr] X=35.9 Y=6 Z=0
    g22: ArcOfCircle CenterX=36.4 CenterY=11.4 CenterZ=0 NormalX=0 NormalY=0 NormalZ=1 AngleXU=0 Radius=0.5 StartAngle=1.5708 EndAngle=3.14159
    g23: GeomPoint [constr] X=35.9 Y=11.9 Z=0
    g24: ArcOfCircle CenterX=36.4 CenterY=20.6 CenterZ=0 NormalX=0 NormalY=0 NormalZ=1 AngleXU=0 Radius=0.5 StartAngle=3.14159 EndAngle=4.71239
    g25: GeomPoint [constr] X=35.9 Y=20.1 Z=0
    g26: ArcOfCircle CenterX=36.4 CenterY=25.5 CenterZ=0 NormalX=0 NormalY=0 NormalZ=1 AngleXU=0 Radius=0.5 StartAngle=1.5708 EndAngle=3.14159
    g27: GeomPoint [constr] X=35.9 Y=26 Z=0
  constraints (66):
    c: Coincident(g0,g-5)
    c: Horizontal(g0)
    c: Coincident(g2,g-11)
    c: Horizontal(g2)
    c: Coincident(g3,g2)
    c: Vertical(g3)
    c: PointOnObject(g21,g-9)
    c: Horizontal(g4)
    c: Vertical(g5)
    c: Horizontal(g6)
    c: Coincident(g7,g6)
    c: Vertical(g7)
    c: Coincident(g8,g7)
    c: Horizontal(g8)
    c: PointOnObject(g27,g-6)
    c: Vertical(g9)
    c: Horizontal(g10)
    c: Vertical(g11)
    c: Coincident(g0,g11)
    c: Vertical(g1)
    c: DistanceY(g21,g23) = 5.9
    c: DistanceY(g25,g27) = 5.9
    c: DistanceX(g23,g25) = 0
    c: PointOnObject(g6,g-14)
    c: DistanceX(g-8,g21) = 0.3
    c: DistanceX(g0,g19) = 8.5
    c: PointOnObject(g13,g10)
    c: PointOnObject(g13,g11)
    c: Tangent(g10,g12) = 1.5708
    c: Tangent(g11,g12) = 1.5708
    c: PointOnObject(g15,g3)
    c: PointOnObject(g15,g4)
    c: Tangent(g3,g14) = 1.5708
    c: Tangent(g4,g14) = 1.5708
    c: PointOnObject(g17,g1)
    c: PointOnObject(g17,g2)
    c: Tangent(g1,g16) = 1.5708
    c: Tangent(g2,g16) = 1.5708
    c: PointOnObject(g19,g0)
    c: PointOnObject(g19,g1)
    c: Tangent(g0,g18) = 1.5708
    c: Tangent(g1,g18) = 1.5708
    c: PointOnObject(g21,g4)
    c: PointOnObject(g21,g5)
    c: Tangent(g4,g20) = 1.5708
    c: Tangent(g5,g20) = 1.5708
    c: PointOnObject(g23,g5)
    c: PointOnObject(g23,g6)
    c: Tangent(g5,g22) = 1.5708
    c: Tangent(g6,g22) = 1.5708
    c: PointOnObject(g25,g8)
    c: PointOnObject(g25,g9)
    c: Tangent(g8,g24) = 1.5708
    c: Tangent(g9,g24) = 1.5708
    c: PointOnObject(g27,g9)
    c: PointOnObject(g27,g10)
    c: Tangent(g9,g26) = 1.5708
    c: Tangent(g10,g26) = 1.5708
    c: Radius(g12) = 1
    c: Radius(g18) = 1
    c: Radius(g16) = 1
    c: Radius(g14) = 1
    c: Radius(g20) = 0.5
    c: Radius(g22) = 0.5
    c: Radius(g24) = 0.5
    c: Radius(g26) = 0.5
FEATURE [PartDesign::Pad] Pad114
  Direction = (0,0,-1)
  Length = 5
  Length2 = 10
  Profile = -> Sketch155
  ReferenceAxis = -> Sketch155 [N_Axis]
  Refine = true
  Suppressed = false
  Type = 0
FEATURE [Sketcher::SketchObject] Sketch156
  ArcFitTolerance = 1e-06
  AttachmentSupport = -> [Pad114]
  ExternalGeometry = -> [Pad114]
  FullyConstrained = true
  MakeInternals = false
  MapMode = 5
  Placement = pos=(0,0,-18.2) rot=(1,0,0;3.14159rad)
  sketch-geometry (12):
    g0: LineSegment StartX=42.3 StartY=20.1 StartZ=0 EndX=36.4 EndY=20.1 EndZ=0
    g1: LineSegment StartX=35.9 StartY=20.6 StartZ=0 EndX=35.9 EndY=25.5 EndZ=0
    g2: LineSegment StartX=42.3 StartY=20.1 StartZ=0 EndX=42.3 EndY=26 EndZ=0
    g3: LineSegment StartX=42.3 StartY=26 StartZ=0 EndX=36.4 EndY=26 EndZ=0
    g4: ArcOfCircle CenterX=36.4 CenterY=25.5 CenterZ=0 NormalX=0 NormalY=0 NormalZ=1 AngleXU=0 Radius=0.5 StartAngle=1.5708 EndAngle=3.14159
    g5: ArcOfCircle CenterX=36.4 CenterY=20.6 CenterZ=0 NormalX=0 NormalY=0 NormalZ=1 AngleXU=0 Radius=0.5 StartAngle=3.14161 EndAngle=4.71239
    g6: ArcOfCircle CenterX=36.4 CenterY=11.4 CenterZ=0 NormalX=0 NormalY=0 NormalZ=1 AngleXU=0 Radius=0.5 StartAngle=1.5708 EndAngle=3.14159
    g7: ArcOfCircle CenterX=36.4 CenterY=6.5 CenterZ=0 NormalX=0 NormalY=0 NormalZ=1 AngleXU=0 Radius=0.5 StartAngle=3.14159 EndAngle=4.71239
    g8: LineSegment StartX=35.9 StartY=6.5 StartZ=0 EndX=35.9 EndY=11.4 EndZ=0
    g9: LineSegment StartX=36.4 StartY=11.9 StartZ=0 EndX=42.3 EndY=11.9 EndZ=0
    g10: LineSegment StartX=42.3 StartY=11.9 StartZ=0 EndX=42.3 EndY=6 EndZ=0
    g11: LineSegment StartX=42.3 StartY=6 StartZ=0 EndX=36.4 EndY=6 EndZ=0
  constraints (28):
    c: Coincident(g0,g-13)
    c: Coincident(g0,g-6)
    c: Coincident(g2,g0)
    c: Vertical(g2)
    c: Coincident(g3,g-7)
    c: Coincident(g3,g2)
    c: PointOnObject(g2,g-3)
    c: Coincident(g4,g3)
    c: Coincident(g4,g1)
    c: Coincident(g5,g1)
    c: Coincident(g5,g0)
    c: PointOnObject(g1,g-5)
    c: Coincident(g4,g-7)
    c: Coincident(g5,g-6)
    c: PointOnObject(g1,g-5)
    c: Coincident(g6,g-10)
    c: Tangent(g6,g-9) = -1.5708
    c: Tangent(g7,g-11) = -1.5708
    c: Coincident(g7,g-12)
    c: Coincident(g8,g7)
    c: Coincident(g8,g6)
    c: Coincident(g9,g6)
    c: Coincident(g9,g-13)
    c: Coincident(g10,g9)
    c: PointOnObject(g10,g-12)
    c: Vertical(g10)
    c: Coincident(g11,g10)
    c: Coincident(g11,g7)
FEATURE [PartDesign::Pocket] Pocket055
  BaseFeature = -> Pad114
  Direction = (0,0,1)
  Length = 2
  Length2 = 5
  Profile = -> Sketch156
  ReferenceAxis = -> Sketch156 [N_Axis]
  Refine = true
  Suppressed = false
  Type = 0
FEATURE [Sketcher::SketchObject] Sketch157
  ArcFitTolerance = 1e-06
  AttachmentSupport = -> [Pocket055]
  ExternalGeometry = -> [Pocket055]
  FullyConstrained = true
  MakeInternals = false
  MapMode = 5
  Placement = pos=(0,0,-18.2) rot=(1,0,0;3.14159rad)
  sketch-geometry (10):
    g0: ArcOfCircle CenterX=49.6 CenterY=25 CenterZ=0 NormalX=0 NormalY=0 NormalZ=1 AngleXU=0 Radius=1 StartAngle=-3.6e-15 EndAngle=1.5708
    g1: ArcOfCircle CenterX=49.6 CenterY=7 CenterZ=0 NormalX=0 NormalY=0 NormalZ=1 AngleXU=0 Radius=1 StartAngle=4.71239 EndAngle=6.28319
    g2: LineSegment StartX=50.6 StartY=10.1 StartZ=0 EndX=50.6 EndY=7 EndZ=0
    g3: LineSegment StartX=49.6 StartY=6 StartZ=0 EndX=42.3 EndY=6 EndZ=0
    g4: LineSegment StartX=50.6 StartY=10.1 StartZ=0 EndX=42.3 EndY=10.1 EndZ=0
    g5: LineSegment StartX=42.3 StartY=10.1 StartZ=0 EndX=42.3 EndY=6 EndZ=0
    g6: LineSegment StartX=50.6 StartY=25 StartZ=0 EndX=50.6 EndY=21.9 EndZ=0
    g7: LineSegment StartX=49.6 StartY=26 StartZ=0 EndX=42.3 EndY=26 EndZ=0
    g8: LineSegment StartX=50.6 StartY=21.9 StartZ=0 EndX=42.3 EndY=21.9 EndZ=0
    g9: LineSegment StartX=42.3 StartY=26 StartZ=0 EndX=42.3 EndY=21.9 EndZ=0
  constraints (22):
    c: Tangent(g0,g-4) = -1.5708
    c: Coincident(g0,g-5)
    c: Tangent(g1,g-8) = -1.5708
    c: Coincident(g1,g-9)
    c: Coincident(g2,g-7)
    c: Coincident(g2,g1)
    c: Coincident(g3,g1)
    c: Coincident(g3,g-9)
    c: Coincident(g4,g2)
    c: PointOnObject(g4,g-6)
    c: Horizontal(g4)
    c: Coincident(g5,g4)
    c: Coincident(g5,g3)
    c: Coincident(g6,g0)
    c: Coincident(g6,g-3)
    c: Coincident(g7,g0)
    c: Coincident(g7,g-6)
    c: Coincident(g8,g6)
    c: PointOnObject(g8,g-6)
    c: Horizontal(g8)
    c: Coincident(g9,g7)
    c: Coincident(g9,g8)
FEATURE [PartDesign::Pocket] Pocket056
  BaseFeature = -> Pocket055
  Direction = (0,0,1)
  Length = 1
  Length2 = 5
  Profile = -> Sketch157
  ReferenceAxis = -> Sketch157 [N_Axis]
  Refine = true
  Suppressed = false
  Type = 0
FEATURE [Sketcher::SketchObject] Sketch158
  ArcFitTolerance = 1e-06
  AttachmentSupport = -> [Pocket056]
  ExternalGeometry = -> [Pocket056]
  FullyConstrained = true
  MakeInternals = false
  MapMode = 5
  Placement = pos=(42.3,0,0) rot=(0.57735,-0.57735,-0.57735;2.0944rad)
  sketch-geometry (6):
    g0: LineSegment StartX=10.1 StartY=-17.2 StartZ=0 EndX=6 EndY=-16.2 EndZ=0
    g1: LineSegment StartX=6 StartY=-16.2 StartZ=0 EndX=6 EndY=-17.2 EndZ=0
    g2: LineSegment StartX=6 StartY=-17.2 StartZ=0 EndX=10.1 EndY=-17.2 EndZ=0
    g3: LineSegment StartX=21.9 StartY=-17.2 StartZ=0 EndX=26 EndY=-16.2 EndZ=0
    g4: LineSegment StartX=26 StartY=-16.2 StartZ=0 EndX=26 EndY=-17.2 EndZ=0
    g5: LineSegment StartX=26 StartY=-17.2 StartZ=0 EndX=21.9 EndY=-17.2 EndZ=0
  constraints (12):
    c: Coincident(g0,g-4)
    c: Coincident(g0,g-3)
    c: Coincident(g1,g0)
    c: Coincident(g1,g-4)
    c: Coincident(g2,g1)
    c: Coincident(g2,g0)
    c: Coincident(g3,g-5)
    c: Coincident(g3,g-6)
    c: Coincident(g4,g3)
    c: Coincident(g4,g-6)
    c: Coincident(g5,g4)
    c: Coincident(g5,g3)
FEATURE [PartDesign::Pocket] Pocket057
  BaseFeature = -> Pocket056
  Direction = (1,0,0)
  Length = 9
  Length2 = 5
  Profile = -> Sketch158
  ReferenceAxis = -> Sketch158 [N_Axis]
  Refine = true
  Suppressed = false
  Type = 0
FEATURE [Sketcher::SketchObject] Sketch159
  ArcFitTolerance = 1e-06
  AttachmentSupport = -> [Pocket057]
  ExternalGeometry = -> [Pocket057]
  FullyConstrained = true
  MakeInternals = false
  MapMode = 5
  Placement = pos=(0,-10.1,0) rot=(0,0.707107,0.707107;3.14159rad)
  sketch-geometry (4):
    g0: LineSegment [constr] StartX=-50.6 StartY=-16.4439 StartZ=0 EndX=-50.6 EndY=-18.2 EndZ=0
    g1: LineSegment StartX=-50.6 StartY=-18.2 StartZ=0 EndX=-59.1 EndY=-16.2 EndZ=0
    g2: LineSegment StartX=-59.1 StartY=-16.2 StartZ=0 EndX=-59.1 EndY=-18.2 EndZ=0
    g3: LineSegment StartX=-59.1 StartY=-18.2 StartZ=0 EndX=-50.6 EndY=-18.2 EndZ=0
  constraints (10):
    c: Coincident(g0,g-3)
    c: PointOnObject(g0,g-4)
    c: Vertical(g0)
    c: Coincident(g1,g0)
    c: PointOnObject(g1,g-6)
    c: Coincident(g2,g1)
    c: Coincident(g2,g-6)
    c: Coincident(g3,g2)
    c: Coincident(g3,g0)
    c: DistanceY(g2,g2) = 2
FEATURE [PartDesign::Pocket] Pocket058
  BaseFeature = -> Pocket057
  Direction = (0,-1,2e-16)
  Length = 12
  Length2 = 5
  Profile = -> Sketch159
  ReferenceAxis = -> Sketch159 [N_Axis]
  Refine = true
  Suppressed = false
  Type = 0
FEATURE [Sketcher::SketchObject] Sketch160
  ArcFitTolerance = 1e-06
  AttachmentSupport = -> [Pocket058]
  ExternalGeometry = -> [Pocket058]
  FullyConstrained = true
  MakeInternals = false
  MapMode = 5
  Placement = pos=(0,0,-18.2) rot=(1,0,0;3.14159rad)
  sketch-geometry (4):
    g0: LineSegment StartX=59.1 StartY=20.4 StartZ=0 EndX=57.1 EndY=20.4 EndZ=0
    g1: LineSegment StartX=57.1 StartY=20.4 StartZ=0 EndX=57.1 EndY=11.6 EndZ=0
    g2: LineSegment StartX=57.1 StartY=11.6 StartZ=0 EndX=59.1 EndY=11.6 EndZ=0
    g3: LineSegment StartX=59.1 StartY=11.6 StartZ=0 EndX=59.1 EndY=20.4 EndZ=0
  constraints (12):
    c: Coincident(g0,g1)
    c: Coincident(g1,g2)
    c: Coincident(g2,g3)
    c: Coincident(g3,g0)
    c: Horizontal(g0)
    c: Horizontal(g2)
    c: Vertical(g1)
    c: Vertical(g3)
    c: PointOnObject(g0,g-4)
    c: DistanceY(g-5,g1) = 1.5
    c: DistanceY(g0,g-3) = 1.5
    c: DistanceX(g0,g0) = 2
FEATURE [PartDesign::Pocket] Pocket059
  BaseFeature = -> Pocket058
  Direction = (0,0,1)
  Length = 5
  Length2 = 5
  Profile = -> Sketch160
  ReferenceAxis = -> Sketch160 [N_Axis]
  Refine = true
  Suppressed = false
  Type = 0
FEATURE [Sketcher::SketchObject] Sketch161
  ArcFitTolerance = 1e-06
  AttachmentOffset = pos=(0,0,-1.5) rot=(0,0,1;0rad)
  AttachmentSupport = -> [Pocket059]
  ExternalGeometry = -> [Pocket059]
  FullyConstrained = true
  MakeInternals = false
  MapMode = 5
  Placement = pos=(0,-11.6,3e-16) rot=(0,0.707107,0.707107;3.14159rad)
  sketch-geometry (4):
    g0: LineSegment StartX=-50.6 StartY=-13.2 StartZ=0 EndX=-57.1 EndY=-13.2 EndZ=0
    g1: LineSegment StartX=-57.1 StartY=-13.2 StartZ=0 EndX=-57.1 EndY=-14.7706 EndZ=0
    g2: LineSegment StartX=-50.6 StartY=-13.2 StartZ=0 EndX=-50.6 EndY=-16.3 EndZ=0
    g3: LineSegment StartX=-50.6 StartY=-16.3 StartZ=0 EndX=-57.1 EndY=-14.7706 EndZ=0
  constraints (10):
    c: Coincident(g0,g-6)
    c: Coincident(g0,g-5)
    c: Coincident(g1,g0)
    c: Coincident(g2,g0)
    c: Vertical(g2)
    c: Coincident(g3,g2)
    c: Coincident(g3,g1)
    c: Parallel(g3,g-3)
    c: DistanceY(g-5,g1) = 1.9
    c: PointOnObject(g1,g-5)
FEATURE [PartDesign::Pocket] Pocket060
  BaseFeature = -> Pocket059
  Direction = (0,-1,2e-16)
  Length = 8.8
  Length2 = 5
  Profile = -> Sketch161
  ReferenceAxis = -> Sketch161 [N_Axis]
  Refine = true
  Suppressed = false
  Type = 0
FEATURE [Sketcher::SketchObject] Sketch162
  ArcFitTolerance = 1e-06
  AttachmentSupport = -> [Pocket060]
  ExternalGeometry = -> [Pocket060]
  FullyConstrained = true
  MakeInternals = false
  MapMode = 5
  Placement = pos=(0,0,-13.2) rot=(0,0,1;0rad)
  sketch-geometry (7):
    g0: ArcOfCircle CenterX=58.1 CenterY=-20.9 CenterZ=0 NormalX=0 NormalY=0 NormalZ=1 AngleXU=0 Radius=1 StartAngle=3.14159 EndAngle=6.28319
    g1: LineSegment [constr] StartX=58.1 StartY=-20.9 StartZ=0 EndX=57.1 EndY=-20.9 EndZ=0
    g2: ArcOfCircle CenterX=58.1 CenterY=-11.1 CenterZ=0 NormalX=0 NormalY=0 NormalZ=1 AngleXU=0 Radius=1 StartAngle=4.303e-13 EndAngle=3.14159
    g3: LineSegment [constr] StartX=58.1 StartY=-11.1 StartZ=0 EndX=57.1 EndY=-11.1 EndZ=0
    g4: LineSegment StartX=59.1 StartY=-11.1 StartZ=0 EndX=59.1 EndY=-20.9 EndZ=0
    g5: LineSegment StartX=57.1 StartY=-20.9 StartZ=0 EndX=57.1 EndY=-11.1 EndZ=0
    g6: LineSegment [constr] StartX=58.1 StartY=-11.1 StartZ=0 EndX=59.1 EndY=-11.1 EndZ=0
  constraints (15):
    c: Coincident(g0,g-8)
    c: Coincident(g0,g-7)
    c: Coincident(g1,g0)
    c: Coincident(g1,g0)
    c: Horizontal(g1)
    c: Coincident(g3,g2)
    c: Coincident(g3,g2)
    c: Coincident(g2,g-3)
    c: Coincident(g4,g2)
    c: Tangent(g4,g0) = 1.5708
    c: Coincident(g5,g0)
    c: Tangent(g5,g2) = 1.5708
    c: Coincident(g6,g2)
    c: Coincident(g6,g2)
    c: Horizontal(g6)
FEATURE [PartDesign::Pad] Pad115
  BaseFeature = -> Pocket060
  Direction = (0,0,1)
  Length = 1.5
  Length2 = 10
  Profile = -> Sketch162
  ReferenceAxis = -> Sketch162 [N_Axis]
  Refine = true
  Suppressed = false
  Type = 0
FEATURE [PartDesign::Pocket] Pocket061
  BaseFeature = -> Pad115
  Direction = (0,0,1)
  Length = 0.05
  Length2 = 5
  Profile = -> Pad115 [Face30]
  Refine = true
  Suppressed = false
  Type = 0
FEATURE [Sketcher::SketchObject] Sketch163
  ArcFitTolerance = 1e-06
  AttachmentSupport = -> [Pocket061]
  ExternalGeometry = -> [Pocket061]
  FullyConstrained = true
  MakeInternals = false
  MapMode = 5
  Placement = pos=(0,0,-18.2) rot=(1,0,0;3.14159rad)
  sketch-geometry (1):
    g0: Circle CenterX=46.45 CenterY=16 CenterZ=0 NormalX=0 NormalY=0 NormalZ=1 AngleXU=0 Radius=1
  constraints (3):
    c: Diameter(g0) = 2
    c: DistanceX(g-4,g0) = 4.15
    c: DistanceY(g0,g-4) = 5.9
FEATURE [PartDesign::Pocket] Pocket062
  BaseFeature = -> Pocket061
  Direction = (0,0,1)
  Length = 5
  Length2 = 5
  Profile = -> Sketch163
  ReferenceAxis = -> Sketch163 [N_Axis]
  Refine = true
  Suppressed = false
  Type = 0
FEATURE [Sketcher::SketchObject] Sketch164
  ArcFitTolerance = 1e-06
  AttachmentSupport = -> [Pocket062]
  ExternalGeometry = -> [Pocket062]
  FullyConstrained = true
  MakeInternals = false
  MapMode = 5
  Placement = pos=(0,0,-18.2) rot=(1,0,0;3.14159rad)
  sketch-geometry (1):
    g0: Circle CenterX=46.45 CenterY=16 CenterZ=0 NormalX=0 NormalY=0 NormalZ=1 AngleXU=0 Radius=1.95
  constraints (2):
    c: Coincident(g0,g-3)
    c: Diameter(g0) = 3.9
FEATURE [PartDesign::Pocket] Pocket063
  BaseFeature = -> Pocket062
  Direction = (0,0,1)
  Length = 1.5
  Length2 = 5
  Profile = -> Sketch164
  ReferenceAxis = -> Sketch164 [N_Axis]
  Refine = true
  Suppressed = false
  Type = 0
FEATURE [Sketcher::SketchObject] Sketch165
  ArcFitTolerance = 1e-06
  AttachmentSupport = -> [Pocket063]
  ExternalGeometry = -> [Pocket063]
  FullyConstrained = true
  MakeInternals = false
  MapMode = 5
  Placement = pos=(0,0,-13.2) rot=(0,0,1;0rad)
  sketch-geometry (4):
    g0: LineSegment StartX=50.6 StartY=-11.6 StartZ=0 EndX=43.8 EndY=-11.6 EndZ=0
    g1: LineSegment StartX=43.8 StartY=-11.6 StartZ=0 EndX=43.8 EndY=-20.4 EndZ=0
    g2: LineSegment StartX=43.8 StartY=-20.4 StartZ=0 EndX=50.6 EndY=-20.4 EndZ=0
    g3: LineSegment StartX=50.6 StartY=-20.4 StartZ=0 EndX=50.6 EndY=-11.6 EndZ=0
  constraints (10):
    c: Coincident(g0,g1)
    c: Coincident(g1,g2)
    c: Coincident(g2,g3)
    c: Coincident(g3,g0)
    c: Horizontal(g0)
    c: Horizontal(g2)
    c: Vertical(g1)
    c: Coincident(g0,g-3)
    c: Coincident(g2,g-3)
    c: DistanceX(g-4,g1) = 1.5
FEATURE [PartDesign::Pocket] Pocket064
  BaseFeature = -> Pocket063
  Direction = (0,0,-1)
  Length = 3.1
  Length2 = 5
  Profile = -> Sketch165
  ReferenceAxis = -> Sketch165 [N_Axis]
  Refine = true
  Suppressed = false
  Type = 0
FEATURE [Sketcher::SketchObject] Sketch166
  ArcFitTolerance = 1e-06
  AttachmentSupport = -> [Pocket064]
  ExternalGeometry = -> [Pocket064]
  FullyConstrained = true
  MakeInternals = false
  MapMode = 5
  Placement = pos=(0,0,-13.2) rot=(0,0,1;0rad)
  sketch-geometry (8):
    g0: LineSegment StartX=42.3 StartY=-10.4 StartZ=0 EndX=42.3 EndY=-7.5 EndZ=0
    g1: LineSegment StartX=42.3 StartY=-7.5 StartZ=0 EndX=37.4 EndY=-7.5 EndZ=0
    g2: LineSegment StartX=37.4 StartY=-7.5 StartZ=0 EndX=37.4 EndY=-10.4 EndZ=0
    g3: LineSegment StartX=37.4 StartY=-10.4 StartZ=0 EndX=42.3 EndY=-10.4 EndZ=0
    g4: LineSegment StartX=37.4 StartY=-21.6 StartZ=0 EndX=37.4 EndY=-24.5 EndZ=0
    g5: LineSegment StartX=37.4 StartY=-24.5 StartZ=0 EndX=42.3 EndY=-24.5 EndZ=0
    g6: LineSegment StartX=42.3 StartY=-24.5 StartZ=0 EndX=42.3 EndY=-21.6 EndZ=0
    g7: LineSegment StartX=42.3 StartY=-21.6 StartZ=0 EndX=37.4 EndY=-21.6 EndZ=0
  constraints (24):
    c: Coincident(g0,g1)
    c: Coincident(g1,g2)
    c: Coincident(g2,g3)
    c: Coincident(g3,g0)
    c: Vertical(g0)
    c: Vertical(g2)
    c: Horizontal(g1)
    c: Horizontal(g3)
    c: DistanceX(g-6,g0) = 0
    c: DistanceX(g-7,g2) = 1.5
    c: DistanceY(g1,g-8) = 1.5
    c: DistanceY(g-6,g2) = 1.5
    c: Coincident(g4,g5)
    c: Coincident(g5,g6)
    c: Coincident(g6,g7)
    c: Coincident(g7,g4)
    c: Vertical(g4)
    c: Vertical(g6)
    c: Horizontal(g5)
    c: Horizontal(g7)
    c: DistanceX(g6,g-3) = 0
    c: DistanceX(g-5,g4) = 1.5
    c: DistanceY(g4,g-3) = 1.5
    c: DistanceY(g-4,g4) = 1.5
FEATURE [PartDesign::Pocket] Pocket065
  BaseFeature = -> Pocket064
  Direction = (0,0,-1)
  Length = 1.5
  Length2 = 5
  Profile = -> Sketch166
  ReferenceAxis = -> Sketch166 [N_Axis]
  Refine = true
  Suppressed = false
  Type = 0
FEATURE [Sketcher::SketchObject] Sketch167
  ArcFitTolerance = 1e-06
  AttachmentOffset = pos=(0,0,-1.5) rot=(0,0,1;0rad)
  AttachmentSupport = -> [Pocket065]
  ExternalGeometry = -> [Pocket065]
  FullyConstrained = true
  MakeInternals = false
  MapMode = 5
  Placement = pos=(49.1,0,0) rot=(0.57735,0.57735,0.57735;2.0944rad)
  sketch-geometry (8):
    g0: LineSegment StartX=-24.5 StartY=-13.2 StartZ=0 EndX=-20.4 EndY=-13.2 EndZ=0
    g1: LineSegment StartX=-24.5 StartY=-13.2 StartZ=0 EndX=-24.5 EndY=-14.9439 EndZ=0
    g2: LineSegment StartX=-20.4 StartY=-16.3 StartZ=0 EndX=-20.4 EndY=-13.2 EndZ=0
    g3: LineSegment StartX=-24.5 StartY=-14.9439 StartZ=0 EndX=-20.4 EndY=-16.3 EndZ=0
    g4: LineSegment StartX=-7.5 StartY=-13.2 StartZ=0 EndX=-7.5 EndY=-14.9439 EndZ=0
    g5: LineSegment StartX=-7.5 StartY=-14.9439 StartZ=0 EndX=-11.6 EndY=-16.3 EndZ=0
    g6: LineSegment StartX=-11.6 StartY=-16.3 StartZ=0 EndX=-11.6 EndY=-13.2 EndZ=0
    g7: LineSegment StartX=-11.6 StartY=-13.2 StartZ=0 EndX=-7.5 EndY=-13.2 EndZ=0
  constraints (20):
    c: Coincident(g0,g-7)
    c: PointOnObject(g0,g-9)
    c: Horizontal(g0)
    c: Coincident(g1,g0)
    c: Vertical(g1)
    c: Coincident(g2,g0)
    c: DistanceY(g-4,g1) = 1.5
    c: Coincident(g3,g1)
    c: Coincident(g3,g-13)
    c: Coincident(g2,g3)
    c: Coincident(g4,g-8)
    c: Vertical(g4)
    c: Coincident(g5,g4)
    c: Coincident(g5,g-12)
    c: Coincident(g6,g5)
    c: PointOnObject(g6,g-10)
    c: Coincident(g7,g6)
    c: Coincident(g7,g4)
    c: Horizontal(g7)
    c: DistanceY(g-6,g4) = 1.5
FEATURE [PartDesign::Pocket] Pocket066
  BaseFeature = -> Pocket065
  Direction = (-1,0,0)
  Length = 5.3
  Length2 = 5
  Profile = -> Sketch167
  ReferenceAxis = -> Sketch167 [N_Axis]
  Refine = true
  Suppressed = false
  Type = 0
FEATURE [PartDesign::Pocket] Pocket067
  BaseFeature = -> Pocket066
  Direction = (1,0,0)
  Length = 2
  Length2 = 5
  Profile = -> Pocket066 [Face42,Face43]
  Refine = true
  Suppressed = false
  Type = 0
FEATURE [Sketcher::SketchObject] Sketch168
  ArcFitTolerance = 1e-06
  AttachmentSupport = -> [Pocket067]
  ExternalGeometry = -> [Pocket067]
  FullyConstrained = true
  MakeInternals = false
  MapMode = 5
  Placement = pos=(0,-10.1,0) rot=(0,0.707107,0.707107;3.14159rad)
  sketch-geometry (2):
    g0: ArcOfCircle CenterX=-53.7 CenterY=-13.2 CenterZ=0 NormalX=0 NormalY=0 NormalZ=1 AngleXU=0 Radius=1.5 StartAngle=3.14159 EndAngle=6.28319
    g1: LineSegment StartX=-55.2 StartY=-13.2 StartZ=0 EndX=-52.2 EndY=-13.2 EndZ=0
  constraints (7):
    c: PointOnObject(g0,g-3)
    c: PointOnObject(g0,g-3)
    c: PointOnObject(g0,g-3)
    c: Radius(g0) = 1.5
    c: DistanceX(g-3,g0) = 2.9
    c: Coincident(g1,g0)
    c: Coincident(g1,g0)
FEATURE [PartDesign::Pocket] Pocket068
  BaseFeature = -> Pocket067
  Direction = (0,-1,2e-16)
  Length = 13
  Length2 = 5
  Profile = -> Sketch168
  ReferenceAxis = -> Sketch168 [N_Axis]
  Refine = true
  Suppressed = false
  Type = 0
FEATURE [Sketcher::SketchObject] Sketch169
  ArcFitTolerance = 1e-06
  AttachmentSupport = -> [Pocket068]
  ExternalGeometry = -> [Pocket068]
  FullyConstrained = true
  MakeInternals = false
  MapMode = 5
  Placement = pos=(0,-11.9,0) rot=(1,0,0;1.5708rad)
  sketch-geometry (2):
    g0: ArcOfCircle CenterX=39.55 CenterY=-13.2 CenterZ=0 NormalX=0 NormalY=0 NormalZ=1 AngleXU=0 Radius=1.25 StartAngle=3.14159 EndAngle=6.28319
    g1: LineSegment StartX=40.8 StartY=-13.2 StartZ=0 EndX=38.3 EndY=-13.2 EndZ=0
  constraints (7):
    c: PointOnObject(g0,g-3)
    c: PointOnObject(g0,g-3)
    c: Radius(g0) = 1.25
    c: PointOnObject(g0,g-3)
    c: DistanceX(g-3,g0) = 1.9
    c: Coincident(g1,g0)
    c: Coincident(g1,g0)
FEATURE [PartDesign::Pocket] Pocket069
  BaseFeature = -> Pocket068
  Direction = (0,1,-2e-16)
  Length = 2
  Length2 = 5
  Profile = -> Sketch169
  ReferenceAxis = -> Sketch169 [N_Axis]
  Refine = true
  Suppressed = false
  Type = 0
FEATURE [PartDesign::Pocket] Pocket070
  BaseFeature = -> Pocket069
  Direction = (0,1,-2e-16)
  Length = 10
  Length2 = 5
  Profile = -> Sketch169
  ReferenceAxis = -> Sketch169 [N_Axis]
  Refine = true
  Reversed = true
  Suppressed = false
  Type = 0
FEATURE [Sketcher::SketchObject] Sketch170
  ArcFitTolerance = 1e-06
  AttachmentSupport = -> [Pocket070]
  ExternalGeometry = -> [Pocket070]
  FullyConstrained = true
  MakeInternals = false
  MapMode = 5
  Placement = pos=(0,0,-16.3) rot=(0,0,1;0rad)
  sketch-geometry (2):
    g0: Circle CenterX=46.45 CenterY=-16 CenterZ=0 NormalX=0 NormalY=0 NormalZ=1 AngleXU=0 Radius=3.95
    g1: Circle CenterX=46.45 CenterY=-16 CenterZ=0 NormalX=0 NormalY=0 NormalZ=1 AngleXU=0 Radius=1.00001
  constraints (4):
    c: Coincident(g0,g-3)
    c: Coincident(g1,g0)
    c: Tangent(g1,g-3)
    c: Diameter(g0) = 7.9
FEATURE [PartDesign::Pad] Pad116
  BaseFeature = -> Pocket070
  Direction = (0,0,1)
  Length = 3.1
  Length2 = 10
  Profile = -> Sketch170
  ReferenceAxis = -> Sketch170 [N_Axis]
  Refine = true
  Suppressed = false
  Type = 0
FEATURE [Sketcher::SketchObject] Sketch171
  ArcFitTolerance = 1e-06
  AttachmentSupport = -> [Pad116]
  ExternalGeometry = -> [Pad116]
  FullyConstrained = true
  MakeInternals = false
  MapMode = 5
  Placement = pos=(5.8e-15,0,-13.2) rot=(0,0,1;0rad)
  sketch-geometry (1):
    g0: Circle CenterX=46.45 CenterY=-16 CenterZ=0 NormalX=0 NormalY=0 NormalZ=1 AngleXU=0 Radius=2.4
  constraints (2):
    c: Coincident(g0,g-3)
    c: Diameter(g0) = 4.8
FEATURE [PartDesign::Pocket] Pocket071
  BaseFeature = -> Pad116
  Direction = (0,0,-1)
  Length = 2.05
  Length2 = 5
  Profile = -> Sketch171
  ReferenceAxis = -> Sketch171 [N_Axis]
  Refine = true
  Suppressed = false
  Type = 0
FEATURE [PartDesign::Body] Body006  label="Front_Cover"
  AllowCompound = false
  Group = -> [Binder003,Sketch155,Pad114,Sketch156,Pocket055,Sketch157,Pocket056,Sketch158,Pocket057,Sketch159,Pocket058,Sketch160,Pocket059,Sketch161,Pocket060,Sketch162,Pad115,Pocket061,Sketch163,Pocket062,Sketch164,Pocket063,Sketch165,Pocket064,Sketch166,Pocket065,Sketch167,Pocket066,Pocket067,Sketch168,Pocket068,Sketch169,Pocket069,Pocket070,Sketch170,Pad116,Sketch171,Pocket071]
  Origin = -> Origin006
  Tip = -> Pocket071
